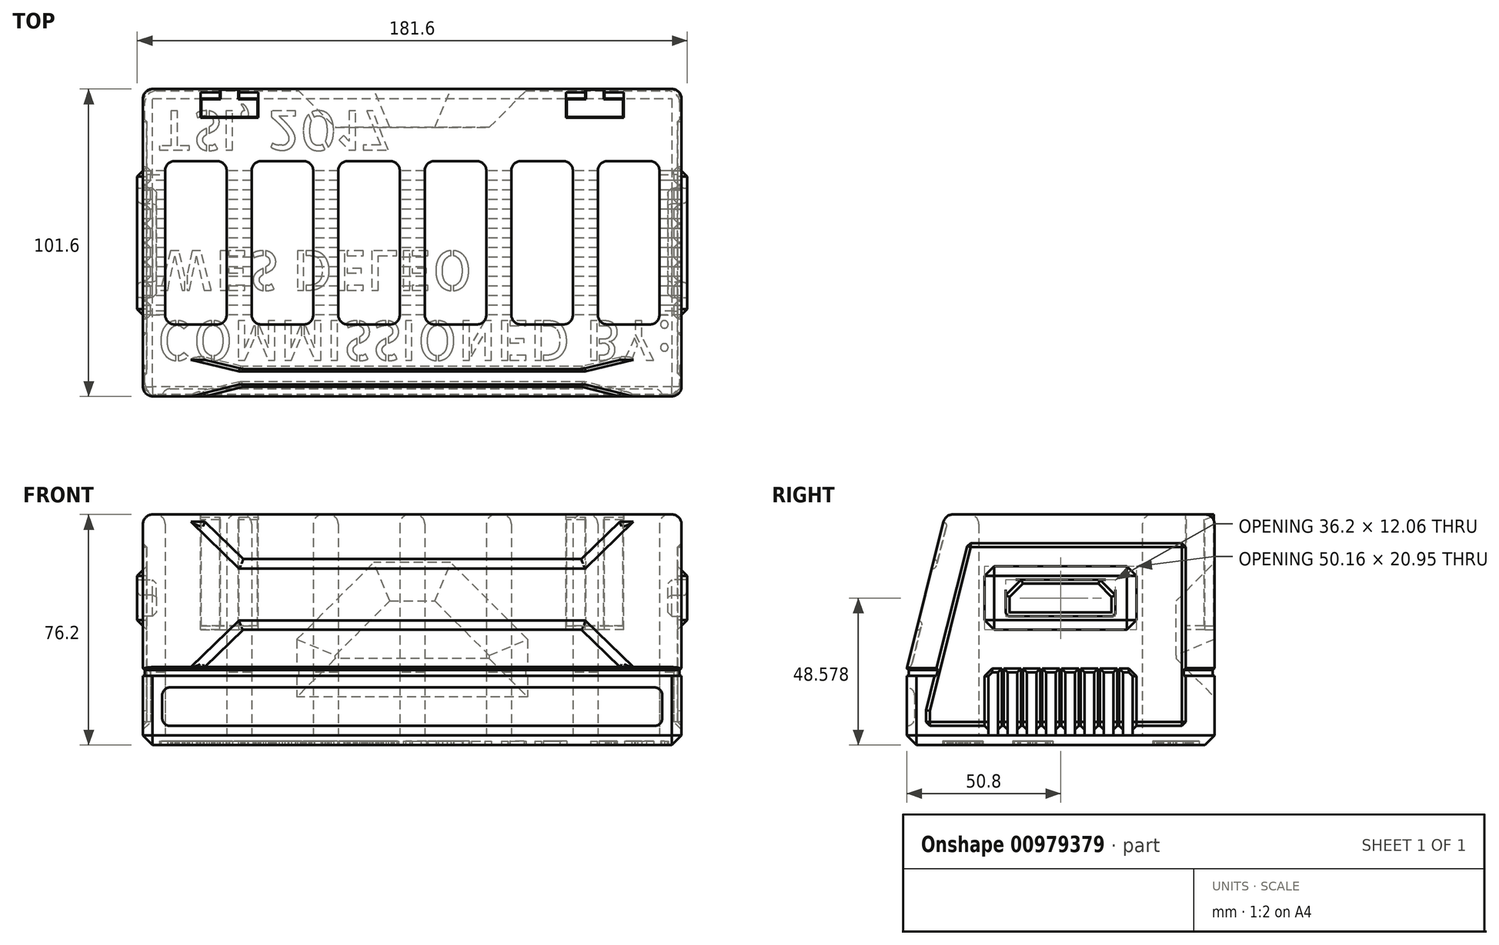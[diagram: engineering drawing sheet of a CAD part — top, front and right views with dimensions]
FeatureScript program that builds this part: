
annotation { "Feature Type Name" : "Feature", "Feature Type Description" : "" }
export const myFeature = defineFeature(function(context is Context, id is Id, definition is map)
    precondition{}
    {
        {
            var Q0;
            Q0=qCreatedBy(makeId("Top.planeOp"),FACE);
            var sketch = newSketch(context, id + "F0", { "sketchPlane" : qUnion([Q0])});
            skLineSegment(sketch, "E0.bottom", {"start": v(-81.6, 26.99) * mm, "end": v(-61.28, 26.99) * mm});
            skLineSegment(sketch, "E0.top", {"start": v(-81.6, -26.99) * mm, "end": v(-61.28, -26.99) * mm});
            skLineSegment(sketch, "E0.left", {"start": v(-81.6, 26.99) * mm, "end": v(-81.6, -26.99) * mm});
            skLineSegment(sketch, "E0.right", {"start": v(-61.28, 26.99) * mm, "end": v(-61.28, -26.99) * mm});
            skLineSegment(sketch, "E1.1.0.0", {"start": v(-53.02, 26.99) * mm, "end": v(-53.02, -26.99) * mm});
            skLineSegment(sketch, "E1.1.0.1", {"start": v(-53.02, 26.99) * mm, "end": v(-32.7, 26.99) * mm});
            skLineSegment(sketch, "E1.1.0.2", {"start": v(-32.7, 26.99) * mm, "end": v(-32.7, -26.99) * mm});
            skLineSegment(sketch, "E1.1.0.3", {"start": v(-53.02, -26.99) * mm, "end": v(-32.7, -26.99) * mm});
            skLineSegment(sketch, "E1.2.0.0", {"start": v(-24.45, 26.99) * mm, "end": v(-24.45, -26.99) * mm});
            skLineSegment(sketch, "E1.2.0.1", {"start": v(-24.45, 26.99) * mm, "end": v(-4.13, 26.99) * mm});
            skLineSegment(sketch, "E1.2.0.2", {"start": v(-4.13, 26.99) * mm, "end": v(-4.13, -26.99) * mm});
            skLineSegment(sketch, "E1.2.0.3", {"start": v(-24.45, -26.99) * mm, "end": v(-4.13, -26.99) * mm});
            skLineSegment(sketch, "E1.3.0.0", {"start": v(4.13, 26.99) * mm, "end": v(4.13, -26.99) * mm});
            skLineSegment(sketch, "E1.3.0.1", {"start": v(4.13, 26.99) * mm, "end": v(24.45, 26.99) * mm});
            skLineSegment(sketch, "E1.3.0.2", {"start": v(24.45, 26.99) * mm, "end": v(24.45, -26.99) * mm});
            skLineSegment(sketch, "E1.3.0.3", {"start": v(4.13, -26.99) * mm, "end": v(24.45, -26.99) * mm});
            skLineSegment(sketch, "E1.4.0.0", {"start": v(32.7, 26.99) * mm, "end": v(32.7, -26.99) * mm});
            skLineSegment(sketch, "E1.4.0.1", {"start": v(32.7, 26.99) * mm, "end": v(53.02, 26.99) * mm});
            skLineSegment(sketch, "E1.4.0.2", {"start": v(53.02, 26.99) * mm, "end": v(53.02, -26.99) * mm});
            skLineSegment(sketch, "E1.4.0.3", {"start": v(32.7, -26.99) * mm, "end": v(53.02, -26.99) * mm});
            skLineSegment(sketch, "E1.direction1", {"start": v(-81.6, -26.99) * mm, "end": v(-53.02, -26.99) * mm, "construction": true});
            skLineSegment(sketch, "E2.0.5.0", {"start": v(61.28, 26.99) * mm, "end": v(61.28, -26.99) * mm});
            skLineSegment(sketch, "E2.3.5.0", {"start": v(61.28, 26.99) * mm, "end": v(81.6, 26.99) * mm});
            skLineSegment(sketch, "E2.6.5.0", {"start": v(81.6, 26.99) * mm, "end": v(81.6, -26.99) * mm});
            skLineSegment(sketch, "E2.9.5.0", {"start": v(61.28, -26.99) * mm, "end": v(81.6, -26.99) * mm});
            skLineSegment(sketch, "E3.bottom", {"start": v(-88.9, 50.8) * mm, "end": v(88.9, 50.8) * mm});
            skLineSegment(sketch, "E3.top", {"start": v(-88.9, -50.8) * mm, "end": v(88.9, -50.8) * mm});
            skLineSegment(sketch, "E3.left", {"start": v(-88.9, 50.8) * mm, "end": v(-88.9, -50.8) * mm});
            skLineSegment(sketch, "E3.right", {"start": v(88.9, 50.8) * mm, "end": v(88.9, -50.8) * mm});
            skSolve(sketch);
        }
        {
            var Q0;
            Q0 = qSketchRegion(id + "F0", true);
            extrude(context, id + "F1", {"entities" : qUnion([Q0]), "depth" : 76.2 * mm, "offsetDistance" : 25.4 * mm});
        }
        {
            var Q0;
            Q0=makeQuery(id+"F1.opExtrude","CAP_EDGE",EDGE,{"disambiguationData":[OSD([sQuery(id+"F0.wireOp",EDGE,"E3.bottom")])],"isStart":false});
            chamfer(context, id + "F2", {"entities" : qUnion([Q0]), "chamferType" : ChamferType.TWO_OFFSETS, "width1" : 50.8 * mm, "oppositeDirection" : false, "width2" : 12.7 * mm, "tangentPropagation" : true});
        }
        {
            var Q0;
            Q0=makeQuery(id+"F1.opExtrude","CAP_FACE",FACE,{"disambiguationData":[OSD([sQuery(id+"F0.wireOp",EDGE,"E0.bottom"),sQuery(id+"F0.wireOp",EDGE,"E0.top"),sQuery(id+"F0.wireOp",EDGE,"E0.left"),sQuery(id+"F0.wireOp",EDGE,"E0.right"),sQuery(id+"F0.wireOp",EDGE,"E1.1.0.0"),sQuery(id+"F0.wireOp",EDGE,"E1.1.0.1"),sQuery(id+"F0.wireOp",EDGE,"E1.1.0.2"),sQuery(id+"F0.wireOp",EDGE,"E1.1.0.3"),sQuery(id+"F0.wireOp",EDGE,"E1.2.0.0"),sQuery(id+"F0.wireOp",EDGE,"E1.2.0.1"),sQuery(id+"F0.wireOp",EDGE,"E1.2.0.2"),sQuery(id+"F0.wireOp",EDGE,"E1.2.0.3"),sQuery(id+"F0.wireOp",EDGE,"E1.3.0.0"),sQuery(id+"F0.wireOp",EDGE,"E1.3.0.1"),sQuery(id+"F0.wireOp",EDGE,"E1.3.0.2"),sQuery(id+"F0.wireOp",EDGE,"E1.3.0.3"),sQuery(id+"F0.wireOp",EDGE,"E1.4.0.0"),sQuery(id+"F0.wireOp",EDGE,"E1.4.0.1"),sQuery(id+"F0.wireOp",EDGE,"E1.4.0.2"),sQuery(id+"F0.wireOp",EDGE,"E1.4.0.3"),sQuery(id+"F0.wireOp",EDGE,"E2.0.5.0"),sQuery(id+"F0.wireOp",EDGE,"E2.3.5.0"),sQuery(id+"F0.wireOp",EDGE,"E2.6.5.0"),sQuery(id+"F0.wireOp",EDGE,"E2.9.5.0"),sQuery(id+"F0.wireOp",EDGE,"E3.bottom"),sQuery(id+"F0.wireOp",EDGE,"E3.top"),sQuery(id+"F0.wireOp",EDGE,"E3.left"),sQuery(id+"F0.wireOp",EDGE,"E3.right")])],"isStart":true});
            var sketch = newSketch(context, id + "F3", { "sketchPlane" : qUnion([Q0])});
            skLineSegment(sketch, "E4.0", {"start": v(-88.9, 50.8) * mm, "end": v(88.9, 50.8) * mm});
            skLineSegment(sketch, "E5.0", {"start": v(-88.9, -50.8) * mm, "end": v(-88.9, 50.8) * mm});
            skLineSegment(sketch, "E6.0", {"start": v(-88.9, -50.8) * mm, "end": v(88.9, -50.8) * mm});
            skLineSegment(sketch, "E7.0", {"start": v(88.9, -50.8) * mm, "end": v(88.9, 50.8) * mm});
            skSolve(sketch);
        }
        {
            var Q0;
            Q0 = qSketchRegion(id + "F3", true);
            extrude(context, id + "F4", {"entities" : qUnion([Q0]), "operationType" : NewBodyOperationType.ADD, "oppositeDirection" : true, "depth" : 3.17 * mm, "offsetDistance" : 25.4 * mm});
        }
        {
            var Q0;
            Q0=makeQuery(id+"F1.opExtrude","SWEPT_FACE",FACE,{"disambiguationData":[OSD([sQuery(id+"F0.wireOp",EDGE,"E3.right")])]});
            var sketch = newSketch(context, id + "F5", { "sketchPlane" : qUnion([Q0])});
            skLineSegment(sketch, "E8.bottom", {"start": v(-23.81, 24.03) * mm, "end": v(-20.64, 24.03) * mm});
            skLineSegment(sketch, "E8.top", {"start": v(-23.81, 3.17) * mm, "end": v(-20.64, 3.17) * mm});
            skLineSegment(sketch, "E8.left", {"start": v(-23.81, 24.03) * mm, "end": v(-23.81, 3.17) * mm});
            skLineSegment(sketch, "E8.right", {"start": v(-20.64, 24.03) * mm, "end": v(-20.64, 3.18) * mm});
            skLineSegment(sketch, "E9.1.0.0", {"start": v(-17.46, 24.03) * mm, "end": v(-14.29, 24.03) * mm});
            skLineSegment(sketch, "E9.1.0.1", {"start": v(-17.46, 24.03) * mm, "end": v(-17.46, 3.17) * mm});
            skLineSegment(sketch, "E9.1.0.2", {"start": v(-17.46, 3.17) * mm, "end": v(-14.29, 3.17) * mm});
            skLineSegment(sketch, "E9.1.0.3", {"start": v(-14.29, 24.03) * mm, "end": v(-14.29, 3.17) * mm});
            skLineSegment(sketch, "E9.2.0.0", {"start": v(-11.11, 24.03) * mm, "end": v(-7.94, 24.03) * mm});
            skLineSegment(sketch, "E9.2.0.1", {"start": v(-11.11, 24.03) * mm, "end": v(-11.11, 3.17) * mm});
            skLineSegment(sketch, "E9.2.0.2", {"start": v(-11.11, 3.17) * mm, "end": v(-7.94, 3.17) * mm});
            skLineSegment(sketch, "E9.2.0.3", {"start": v(-7.94, 24.03) * mm, "end": v(-7.94, 3.17) * mm});
            skLineSegment(sketch, "E9.direction1", {"start": v(-23.81, 3.17) * mm, "end": v(-17.46, 3.17) * mm, "construction": true});
            skLineSegment(sketch, "E10.0.3.0", {"start": v(-4.76, 24.03) * mm, "end": v(-1.59, 24.03) * mm});
            skLineSegment(sketch, "E10.3.3.0", {"start": v(-4.76, 24.03) * mm, "end": v(-4.76, 3.17) * mm});
            skLineSegment(sketch, "E10.6.3.0", {"start": v(-4.76, 3.17) * mm, "end": v(-1.59, 3.17) * mm});
            skLineSegment(sketch, "E10.9.3.0", {"start": v(-1.59, 24.03) * mm, "end": v(-1.59, 3.18) * mm});
            skLineSegment(sketch, "E10.0.4.0", {"start": v(1.59, 24.03) * mm, "end": v(4.76, 24.03) * mm});
            skLineSegment(sketch, "E10.3.4.0", {"start": v(1.59, 24.03) * mm, "end": v(1.59, 3.17) * mm});
            skLineSegment(sketch, "E10.6.4.0", {"start": v(1.59, 3.17) * mm, "end": v(4.76, 3.17) * mm});
            skLineSegment(sketch, "E10.9.4.0", {"start": v(4.76, 24.03) * mm, "end": v(4.76, 3.18) * mm});
            skLineSegment(sketch, "E10.0.5.0", {"start": v(7.94, 24.03) * mm, "end": v(11.11, 24.03) * mm});
            skLineSegment(sketch, "E10.3.5.0", {"start": v(7.94, 24.03) * mm, "end": v(7.94, 3.17) * mm});
            skLineSegment(sketch, "E10.6.5.0", {"start": v(7.94, 3.17) * mm, "end": v(11.11, 3.17) * mm});
            skLineSegment(sketch, "E10.9.5.0", {"start": v(11.11, 24.03) * mm, "end": v(11.11, 3.18) * mm});
            skLineSegment(sketch, "E11.0.6.0", {"start": v(14.29, 24.03) * mm, "end": v(17.46, 24.03) * mm});
            skLineSegment(sketch, "E11.3.6.0", {"start": v(14.29, 24.03) * mm, "end": v(14.29, 3.17) * mm});
            skLineSegment(sketch, "E11.6.6.0", {"start": v(14.29, 3.17) * mm, "end": v(17.46, 3.17) * mm});
            skLineSegment(sketch, "E11.9.6.0", {"start": v(17.46, 24.03) * mm, "end": v(17.46, 3.18) * mm});
            skLineSegment(sketch, "E11.0.7.0", {"start": v(20.64, 24.03) * mm, "end": v(23.81, 24.03) * mm});
            skLineSegment(sketch, "E11.3.7.0", {"start": v(20.64, 24.03) * mm, "end": v(20.64, 3.17) * mm});
            skLineSegment(sketch, "E11.6.7.0", {"start": v(20.64, 3.17) * mm, "end": v(23.81, 3.17) * mm});
            skLineSegment(sketch, "E11.9.7.0", {"start": v(23.81, 24.03) * mm, "end": v(23.81, 3.18) * mm});
            skSolve(sketch);
        }
        {
            var Q0;
            Q0 = qSketchRegion(id + "F5", true);
            var Q1;
            Q1=makeQuery(id+"F1.opExtrude","SWEPT_FACE",FACE,{"disambiguationData":[OSD([sQuery(id+"F0.wireOp",EDGE,"E3.left")])]});
            extrude(context, id + "F6", {"entities" : qUnion([Q0]), "operationType" : NewBodyOperationType.REMOVE, "endBound" : BoundingType.UP_TO_SURFACE, "oppositeDirection" : true, "depth" : 25.4 * mm, "endBoundEntityFace" : qUnion([Q1]), "offsetDistance" : 25.4 * mm});
        }
        {
            var Q0;
            Q0=makeQuery(id+"F1.opExtrude","CAP_FACE",FACE,{"disambiguationData":[OSD([sQuery(id+"F0.wireOp",EDGE,"E0.bottom"),sQuery(id+"F0.wireOp",EDGE,"E0.top"),sQuery(id+"F0.wireOp",EDGE,"E0.left"),sQuery(id+"F0.wireOp",EDGE,"E0.right"),sQuery(id+"F0.wireOp",EDGE,"E1.1.0.0"),sQuery(id+"F0.wireOp",EDGE,"E1.1.0.1"),sQuery(id+"F0.wireOp",EDGE,"E1.1.0.2"),sQuery(id+"F0.wireOp",EDGE,"E1.1.0.3"),sQuery(id+"F0.wireOp",EDGE,"E1.2.0.0"),sQuery(id+"F0.wireOp",EDGE,"E1.2.0.1"),sQuery(id+"F0.wireOp",EDGE,"E1.2.0.2"),sQuery(id+"F0.wireOp",EDGE,"E1.2.0.3"),sQuery(id+"F0.wireOp",EDGE,"E1.3.0.0"),sQuery(id+"F0.wireOp",EDGE,"E1.3.0.1"),sQuery(id+"F0.wireOp",EDGE,"E1.3.0.2"),sQuery(id+"F0.wireOp",EDGE,"E1.3.0.3"),sQuery(id+"F0.wireOp",EDGE,"E1.4.0.0"),sQuery(id+"F0.wireOp",EDGE,"E1.4.0.1"),sQuery(id+"F0.wireOp",EDGE,"E1.4.0.2"),sQuery(id+"F0.wireOp",EDGE,"E1.4.0.3"),sQuery(id+"F0.wireOp",EDGE,"E2.0.5.0"),sQuery(id+"F0.wireOp",EDGE,"E2.3.5.0"),sQuery(id+"F0.wireOp",EDGE,"E2.6.5.0"),sQuery(id+"F0.wireOp",EDGE,"E2.9.5.0"),sQuery(id+"F0.wireOp",EDGE,"E3.bottom"),sQuery(id+"F0.wireOp",EDGE,"E3.top"),sQuery(id+"F0.wireOp",EDGE,"E3.left"),sQuery(id+"F0.wireOp",EDGE,"E3.right")])],"isStart":false});
            var Q1;
            Q1=makeQuery(id+"F1.opExtrude","SWEPT_EDGE",EDGE,{"disambiguationData":[OSD([sQuery(id+"F0.wireOp",EDGE,"E2.0.5.0"),sQuery(id+"F0.wireOp",EDGE,"E2.9.5.0")])]});
            var Q2;
            Q2=makeQuery(id+"F1.opExtrude","SWEPT_EDGE",EDGE,{"disambiguationData":[OSD([sQuery(id+"F0.wireOp",EDGE,"E1.4.0.0"),sQuery(id+"F0.wireOp",EDGE,"E1.4.0.3")])]});
            var Q3;
            Q3=makeQuery(id+"F1.opExtrude","SWEPT_EDGE",EDGE,{"disambiguationData":[OSD([sQuery(id+"F0.wireOp",EDGE,"E1.3.0.0"),sQuery(id+"F0.wireOp",EDGE,"E1.3.0.3")])]});
            var Q4;
            Q4=makeQuery(id+"F1.opExtrude","SWEPT_EDGE",EDGE,{"disambiguationData":[OSD([sQuery(id+"F0.wireOp",EDGE,"E1.2.0.0"),sQuery(id+"F0.wireOp",EDGE,"E1.2.0.3")])]});
            var Q5;
            Q5=makeQuery(id+"F1.opExtrude","SWEPT_EDGE",EDGE,{"disambiguationData":[OSD([sQuery(id+"F0.wireOp",EDGE,"E1.1.0.0"),sQuery(id+"F0.wireOp",EDGE,"E1.1.0.3")])]});
            var Q6;
            Q6=makeQuery(id+"F1.opExtrude","SWEPT_EDGE",EDGE,{"disambiguationData":[OSD([sQuery(id+"F0.wireOp",EDGE,"E0.top"),sQuery(id+"F0.wireOp",EDGE,"E0.left")])]});
            var Q7;
            Q7=makeQuery(id+"F1.opExtrude","SWEPT_EDGE",EDGE,{"disambiguationData":[OSD([sQuery(id+"F0.wireOp",EDGE,"E0.bottom"),sQuery(id+"F0.wireOp",EDGE,"E0.left")])]});
            var Q8;
            Q8=makeQuery(id+"F1.opExtrude","SWEPT_EDGE",EDGE,{"disambiguationData":[OSD([sQuery(id+"F0.wireOp",EDGE,"E0.bottom"),sQuery(id+"F0.wireOp",EDGE,"E0.right")])]});
            var Q9;
            Q9=makeQuery(id+"F1.opExtrude","SWEPT_EDGE",EDGE,{"disambiguationData":[OSD([sQuery(id+"F0.wireOp",EDGE,"E1.1.0.1"),sQuery(id+"F0.wireOp",EDGE,"E1.1.0.2")])]});
            var Q10;
            Q10=makeQuery(id+"F1.opExtrude","SWEPT_EDGE",EDGE,{"disambiguationData":[OSD([sQuery(id+"F0.wireOp",EDGE,"E1.2.0.1"),sQuery(id+"F0.wireOp",EDGE,"E1.2.0.2")])]});
            var Q11;
            Q11=makeQuery(id+"F1.opExtrude","SWEPT_EDGE",EDGE,{"disambiguationData":[OSD([sQuery(id+"F0.wireOp",EDGE,"E1.3.0.1"),sQuery(id+"F0.wireOp",EDGE,"E1.3.0.2")])]});
            var Q12;
            Q12=makeQuery(id+"F1.opExtrude","SWEPT_EDGE",EDGE,{"disambiguationData":[OSD([sQuery(id+"F0.wireOp",EDGE,"E1.4.0.1"),sQuery(id+"F0.wireOp",EDGE,"E1.4.0.2")])]});
            var Q13;
            Q13=makeQuery(id+"F1.opExtrude","SWEPT_EDGE",EDGE,{"disambiguationData":[OSD([sQuery(id+"F0.wireOp",EDGE,"E2.3.5.0"),sQuery(id+"F0.wireOp",EDGE,"E2.6.5.0")])]});
            var Q14;
            Q14=makeQuery(id+"F1.opExtrude","SWEPT_EDGE",EDGE,{"disambiguationData":[OSD([sQuery(id+"F0.wireOp",EDGE,"E2.6.5.0"),sQuery(id+"F0.wireOp",EDGE,"E2.9.5.0")])]});
            var Q15;
            Q15=makeQuery(id+"F1.opExtrude","SWEPT_EDGE",EDGE,{"disambiguationData":[OSD([sQuery(id+"F0.wireOp",EDGE,"E1.4.0.2"),sQuery(id+"F0.wireOp",EDGE,"E1.4.0.3")])]});
            var Q16;
            Q16=makeQuery(id+"F1.opExtrude","SWEPT_EDGE",EDGE,{"disambiguationData":[OSD([sQuery(id+"F0.wireOp",EDGE,"E1.3.0.2"),sQuery(id+"F0.wireOp",EDGE,"E1.3.0.3")])]});
            var Q17;
            Q17=makeQuery(id+"F1.opExtrude","SWEPT_EDGE",EDGE,{"disambiguationData":[OSD([sQuery(id+"F0.wireOp",EDGE,"E1.2.0.2"),sQuery(id+"F0.wireOp",EDGE,"E1.2.0.3")])]});
            var Q18;
            Q18=makeQuery(id+"F1.opExtrude","SWEPT_EDGE",EDGE,{"disambiguationData":[OSD([sQuery(id+"F0.wireOp",EDGE,"E1.1.0.2"),sQuery(id+"F0.wireOp",EDGE,"E1.1.0.3")])]});
            var Q19;
            Q19=makeQuery(id+"F1.opExtrude","SWEPT_EDGE",EDGE,{"disambiguationData":[OSD([sQuery(id+"F0.wireOp",EDGE,"E0.top"),sQuery(id+"F0.wireOp",EDGE,"E0.right")])]});
            var Q20;
            Q20=makeQuery(id+"F1.opExtrude","SWEPT_EDGE",EDGE,{"disambiguationData":[OSD([sQuery(id+"F0.wireOp",EDGE,"E1.1.0.0"),sQuery(id+"F0.wireOp",EDGE,"E1.1.0.1")])]});
            var Q21;
            Q21=makeQuery(id+"F1.opExtrude","SWEPT_EDGE",EDGE,{"disambiguationData":[OSD([sQuery(id+"F0.wireOp",EDGE,"E1.2.0.0"),sQuery(id+"F0.wireOp",EDGE,"E1.2.0.1")])]});
            var Q22;
            Q22=makeQuery(id+"F1.opExtrude","SWEPT_EDGE",EDGE,{"disambiguationData":[OSD([sQuery(id+"F0.wireOp",EDGE,"E1.3.0.0"),sQuery(id+"F0.wireOp",EDGE,"E1.3.0.1")])]});
            var Q23;
            Q23=makeQuery(id+"F1.opExtrude","SWEPT_EDGE",EDGE,{"disambiguationData":[OSD([sQuery(id+"F0.wireOp",EDGE,"E1.4.0.0"),sQuery(id+"F0.wireOp",EDGE,"E1.4.0.1")])]});
            var Q24;
            Q24=makeQuery(id+"F1.opExtrude","SWEPT_EDGE",EDGE,{"disambiguationData":[OSD([sQuery(id+"F0.wireOp",EDGE,"E2.0.5.0"),sQuery(id+"F0.wireOp",EDGE,"E2.3.5.0")])]});
            var Q25;
            Q25=makeQuery(id+"F2.opChamfer","BLEND_EDGE",EDGE,{"blendedFrom":[makeQuery(id+"F1.opExtrude","CAP_EDGE",EDGE,{"disambiguationData":[OSD([sQuery(id+"F0.wireOp",EDGE,"E3.bottom")])],"isStart":false}),makeQuery(id+"F1.opExtrude","SWEPT_FACE",FACE,{"disambiguationData":[OSD([sQuery(id+"F0.wireOp",EDGE,"E3.right")])]})],"blendedInto":[makeQuery(id+"F1.opExtrude","SWEPT_FACE",FACE,{"disambiguationData":[OSD([sQuery(id+"F0.wireOp",EDGE,"E3.right")])]})]});
            var Q26;
            Q26=makeQuery(id+"F2.opChamfer","BLEND_EDGE",EDGE,{"blendedFrom":[makeQuery(id+"F1.opExtrude","CAP_EDGE",EDGE,{"disambiguationData":[OSD([sQuery(id+"F0.wireOp",EDGE,"E3.bottom")])],"isStart":false}),makeQuery(id+"F1.opExtrude","SWEPT_FACE",FACE,{"disambiguationData":[OSD([sQuery(id+"F0.wireOp",EDGE,"E3.left")])]})],"blendedInto":[makeQuery(id+"F1.opExtrude","SWEPT_FACE",FACE,{"disambiguationData":[OSD([sQuery(id+"F0.wireOp",EDGE,"E3.left")])]})]});
            var Q27;
            Q27=makeQuery(id+"F1.opExtrude","SWEPT_EDGE",EDGE,{"disambiguationData":[OSD([sQuery(id+"F0.wireOp",EDGE,"E3.top"),sQuery(id+"F0.wireOp",EDGE,"E3.right")])]});
            var Q28;
            Q28=makeQuery(id+"F1.opExtrude","SWEPT_EDGE",EDGE,{"disambiguationData":[OSD([sQuery(id+"F0.wireOp",EDGE,"E3.top"),sQuery(id+"F0.wireOp",EDGE,"E3.left")])]});
            fillet(context, id + "F7", {"entities" : qUnion([Q0, Q1, Q2, Q3, Q4, Q5, Q6, Q7, Q8, Q9, Q10, Q11, Q12, Q13, Q14, Q15, Q16, Q17, Q18, Q19, Q20, Q21, Q22, Q23, Q24, Q25, Q26, Q27, Q28]), "radius" : 3.17 * mm, "tangentPropagation" : true, "allowEdgeOverflow" : false});
        }
        {
            var Q0;
            Q0=makeQuery(id+"F1.opExtrude","SWEPT_FACE",FACE,{"disambiguationData":[OSD([sQuery(id+"F0.wireOp",EDGE,"E3.left")])]});
            var sketch = newSketch(context, id + "F8", { "sketchPlane" : qUnion([Q0])});
            skLineSegment(sketch, "E12.0", {"start": v(-30.66, 66.67) * mm, "end": v(-44.45, 11.53) * mm});
            skLineSegment(sketch, "E12.1", {"start": v(41.27, 66.67) * mm, "end": v(-30.66, 66.67) * mm});
            skLineSegment(sketch, "E12.2", {"start": v(-44.45, 11.53) * mm, "end": v(-44.45, 6.35) * mm});
            skLineSegment(sketch, "E12.3", {"start": v(-44.45, 6.35) * mm, "end": v(41.27, 6.35) * mm});
            skLineSegment(sketch, "E12.4", {"start": v(41.27, 6.35) * mm, "end": v(41.27, 66.67) * mm});
            skSolve(sketch);
        }
        {
            var Q0;
            Q0 = qSketchRegion(id + "F8", true);
            extrude(context, id + "F9", {"entities" : qUnion([Q0]), "operationType" : NewBodyOperationType.REMOVE, "oppositeDirection" : true, "depth" : 1.27 * mm, "offsetDistance" : 25.4 * mm});
        }
        {
            var Q0;
            Q0=makeQuery(id+"F9.boolean.opBoolean","COPY",FACE,{"derivedFrom":makeQuery(id+"F9.opExtrude","CAP_FACE",FACE,{"disambiguationData":[OSD([sQuery(id+"F8.wireOp",EDGE,"E12.0"),sQuery(id+"F8.wireOp",EDGE,"E12.1"),sQuery(id+"F8.wireOp",EDGE,"E12.2"),sQuery(id+"F8.wireOp",EDGE,"E12.3"),sQuery(id+"F8.wireOp",EDGE,"E12.4")])],"isStart":false})});
            var Q1;
            {var subQ0=sQuery(id+"F5.wireOp",EDGE,"E11.0.7.0");var subQ1=sQuery(id+"F5.wireOp",EDGE,"E11.9.7.0");Q1=makeQuery(id+"F6.boolean.opBoolean","COPY",EDGE,{"disambiguationData":[TD([makeQuery(id+"F1.opExtrude","SWEPT_FACE",FACE,{"disambiguationData":[OSD([sQuery(id+"F0.wireOp",EDGE,"E0.left")])]})])],"derivedFrom":makeQuery(id+"F6.opExtrude","SWEPT_EDGE",EDGE,{"disambiguationData":[OSD([subQ0,subQ1])]})});}
            var Q2;
            {var subQ0=sQuery(id+"F5.wireOp",EDGE,"E8.bottom");var subQ1=sQuery(id+"F5.wireOp",EDGE,"E8.left");Q2=makeQuery(id+"F6.boolean.opBoolean","COPY",EDGE,{"disambiguationData":[TD([makeQuery(id+"F1.opExtrude","SWEPT_FACE",FACE,{"disambiguationData":[OSD([sQuery(id+"F0.wireOp",EDGE,"E0.left")])]})])],"derivedFrom":makeQuery(id+"F6.opExtrude","SWEPT_EDGE",EDGE,{"disambiguationData":[OSD([subQ0,subQ1])]})});}
            var Q3;
            Q3=makeQuery(id+"F9.boolean.opBoolean","COPY",EDGE,{"derivedFrom":makeQuery(id+"F9.opExtrude","SWEPT_EDGE",EDGE,{"disambiguationData":[OSD([sQuery(id+"F8.wireOp",EDGE,"E12.0"),sQuery(id+"F8.wireOp",EDGE,"E12.1")])]})});
            var Q4;
            Q4=makeQuery(id+"F9.boolean.opBoolean","COPY",EDGE,{"derivedFrom":makeQuery(id+"F9.opExtrude","SWEPT_EDGE",EDGE,{"disambiguationData":[OSD([sQuery(id+"F8.wireOp",EDGE,"E12.1"),sQuery(id+"F8.wireOp",EDGE,"E12.4")])]})});
            var Q5;
            Q5=makeQuery(id+"F9.boolean.opBoolean","COPY",EDGE,{"derivedFrom":makeQuery(id+"F9.opExtrude","SWEPT_EDGE",EDGE,{"disambiguationData":[OSD([sQuery(id+"F8.wireOp",EDGE,"E12.3"),sQuery(id+"F8.wireOp",EDGE,"E12.4")])]})});
            var Q6;
            Q6=makeQuery(id+"F9.boolean.opBoolean","COPY",EDGE,{"derivedFrom":makeQuery(id+"F9.opExtrude","SWEPT_EDGE",EDGE,{"disambiguationData":[OSD([sQuery(id+"F8.wireOp",EDGE,"E12.2"),sQuery(id+"F8.wireOp",EDGE,"E12.3")])]})});
            chamfer(context, id + "F10", {"entities" : qUnion([Q0, Q1, Q2, Q3, Q4, Q5, Q6]), "width" : 1.27 * mm, "tangentPropagation" : true});
        }
        {
            var Q0;
            Q0=makeQuery(id+"F1.opExtrude","SWEPT_FACE",FACE,{"disambiguationData":[OSD([sQuery(id+"F0.wireOp",EDGE,"E3.right")])]});
            var sketch = newSketch(context, id + "F11", { "sketchPlane" : qUnion([Q0])});
            skLineSegment(sketch, "E13.0", {"start": v(44.45, 11.53) * mm, "end": v(30.66, 66.68) * mm});
            skLineSegment(sketch, "E13.1", {"start": v(44.45, 6.35) * mm, "end": v(44.45, 11.53) * mm});
            skLineSegment(sketch, "E13.2", {"start": v(30.66, 66.68) * mm, "end": v(-41.27, 66.68) * mm});
            skLineSegment(sketch, "E13.3", {"start": v(-41.27, 66.68) * mm, "end": v(-41.27, 6.35) * mm});
            skLineSegment(sketch, "E13.4", {"start": v(-41.27, 6.35) * mm, "end": v(44.45, 6.35) * mm});
            skSolve(sketch);
        }
        {
            var Q0;
            Q0 = qSketchRegion(id + "F11", true);
            extrude(context, id + "F12", {"entities" : qUnion([Q0]), "operationType" : NewBodyOperationType.REMOVE, "oppositeDirection" : true, "depth" : 1.27 * mm, "offsetDistance" : 25.4 * mm});
        }
        {
            var Q0;
            Q0=makeQuery(id+"F12.boolean.opBoolean","COPY",FACE,{"derivedFrom":makeQuery(id+"F12.opExtrude","CAP_FACE",FACE,{"disambiguationData":[OSD([sQuery(id+"F11.wireOp",EDGE,"E13.0"),sQuery(id+"F11.wireOp",EDGE,"E13.1"),sQuery(id+"F11.wireOp",EDGE,"E13.2"),sQuery(id+"F11.wireOp",EDGE,"E13.3"),sQuery(id+"F11.wireOp",EDGE,"E13.4")])],"isStart":false})});
            var Q1;
            {var subQ0=sQuery(id+"F5.wireOp",EDGE,"E8.bottom");var subQ1=sQuery(id+"F5.wireOp",EDGE,"E8.left");Q1=makeQuery(id+"F6.boolean.opBoolean","COPY",EDGE,{"disambiguationData":[TD([makeQuery(id+"F1.opExtrude","SWEPT_FACE",FACE,{"disambiguationData":[OSD([sQuery(id+"F0.wireOp",EDGE,"E2.6.5.0")])]})])],"derivedFrom":makeQuery(id+"F6.opExtrude","SWEPT_EDGE",EDGE,{"disambiguationData":[OSD([subQ0,subQ1])]})});}
            var Q2;
            {var subQ0=sQuery(id+"F5.wireOp",EDGE,"E11.0.7.0");var subQ1=sQuery(id+"F5.wireOp",EDGE,"E11.9.7.0");Q2=makeQuery(id+"F6.boolean.opBoolean","COPY",EDGE,{"disambiguationData":[TD([makeQuery(id+"F1.opExtrude","SWEPT_FACE",FACE,{"disambiguationData":[OSD([sQuery(id+"F0.wireOp",EDGE,"E2.6.5.0")])]})])],"derivedFrom":makeQuery(id+"F6.opExtrude","SWEPT_EDGE",EDGE,{"disambiguationData":[OSD([subQ0,subQ1])]})});}
            var Q3;
            Q3=makeQuery(id+"F12.boolean.opBoolean","COPY",EDGE,{"derivedFrom":makeQuery(id+"F12.opExtrude","SWEPT_EDGE",EDGE,{"disambiguationData":[OSD([sQuery(id+"F11.wireOp",EDGE,"E13.2"),sQuery(id+"F11.wireOp",EDGE,"E13.3")])]})});
            var Q4;
            Q4=makeQuery(id+"F12.boolean.opBoolean","COPY",EDGE,{"derivedFrom":makeQuery(id+"F12.opExtrude","SWEPT_EDGE",EDGE,{"disambiguationData":[OSD([sQuery(id+"F11.wireOp",EDGE,"E13.0"),sQuery(id+"F11.wireOp",EDGE,"E13.2")])]})});
            var Q5;
            Q5=makeQuery(id+"F12.boolean.opBoolean","COPY",EDGE,{"derivedFrom":makeQuery(id+"F12.opExtrude","SWEPT_EDGE",EDGE,{"disambiguationData":[OSD([sQuery(id+"F11.wireOp",EDGE,"E13.1"),sQuery(id+"F11.wireOp",EDGE,"E13.4")])]})});
            var Q6;
            Q6=makeQuery(id+"F12.boolean.opBoolean","COPY",EDGE,{"derivedFrom":makeQuery(id+"F12.opExtrude","SWEPT_EDGE",EDGE,{"disambiguationData":[OSD([sQuery(id+"F11.wireOp",EDGE,"E13.3"),sQuery(id+"F11.wireOp",EDGE,"E13.4")])]})});
            chamfer(context, id + "F13", {"entities" : qUnion([Q0, Q1, Q2, Q3, Q4, Q5, Q6]), "width" : 1.27 * mm, "tangentPropagation" : true});
        }
        {
            var Q0;
            Q0=makeQuery(id+"F1.opExtrude","SWEPT_FACE",FACE,{"disambiguationData":[OSD([sQuery(id+"F0.wireOp",EDGE,"E3.bottom")])]});
            var sketch = newSketch(context, id + "F14", { "sketchPlane" : qUnion([Q0])});
            skLineSegment(sketch, "E14.bottom", {"start": v(-82.55, 19.05) * mm, "end": v(82.55, 19.05) * mm});
            skLineSegment(sketch, "E14.top", {"start": v(-82.55, 6.35) * mm, "end": v(82.55, 6.35) * mm});
            skLineSegment(sketch, "E14.left", {"start": v(-82.55, 19.05) * mm, "end": v(-82.55, 6.35) * mm});
            skLineSegment(sketch, "E14.right", {"start": v(82.55, 19.05) * mm, "end": v(82.55, 6.35) * mm});
            skSolve(sketch);
        }
        {
            var Q0;
            Q0=makeQuery(id+"F14.imprint","IMPRINT",FACE,{"disambiguationData":[TD([[makeQuery(id+"F14.imprint","IMPRINT",EDGE,{"derivedFrom":sQuery(id+"F14.wireOp",EDGE,"E14.bottom")}),-1.0]])]});
            extrude(context, id + "F15", {"entities" : qUnion([Q0]), "operationType" : NewBodyOperationType.REMOVE, "oppositeDirection" : true, "depth" : 2.54 * mm, "offsetDistance" : 25.4 * mm});
        }
        {
            var Q0;
            Q0=makeQuery(id+"F15.boolean.opBoolean","COPY",EDGE,{"derivedFrom":makeQuery(id+"F15.opExtrude","SWEPT_EDGE",EDGE,{"disambiguationData":[OSD([sQuery(id+"F14.wireOp",EDGE,"E14.bottom"),sQuery(id+"F14.wireOp",EDGE,"E14.left")])]})});
            var Q1;
            Q1=makeQuery(id+"F15.boolean.opBoolean","COPY",EDGE,{"derivedFrom":makeQuery(id+"F15.opExtrude","SWEPT_EDGE",EDGE,{"disambiguationData":[OSD([sQuery(id+"F14.wireOp",EDGE,"E14.bottom"),sQuery(id+"F14.wireOp",EDGE,"E14.right")])]})});
            var Q2;
            Q2=makeQuery(id+"F15.boolean.opBoolean","COPY",FACE,{"derivedFrom":makeQuery(id+"F15.opExtrude","CAP_FACE",FACE,{"disambiguationData":[OSD([sQuery(id+"F14.wireOp",EDGE,"E14.bottom"),sQuery(id+"F14.wireOp",EDGE,"E14.top"),sQuery(id+"F14.wireOp",EDGE,"E14.left"),sQuery(id+"F14.wireOp",EDGE,"E14.right")])],"isStart":false})});
            var Q3;
            Q3=makeQuery(id+"F15.boolean.opBoolean","COPY",EDGE,{"derivedFrom":makeQuery(id+"F15.opExtrude","SWEPT_EDGE",EDGE,{"disambiguationData":[OSD([sQuery(id+"F14.wireOp",EDGE,"E14.top"),sQuery(id+"F14.wireOp",EDGE,"E14.left")])]})});
            var Q4;
            Q4=makeQuery(id+"F15.boolean.opBoolean","COPY",EDGE,{"derivedFrom":makeQuery(id+"F15.opExtrude","SWEPT_EDGE",EDGE,{"disambiguationData":[OSD([sQuery(id+"F14.wireOp",EDGE,"E14.top"),sQuery(id+"F14.wireOp",EDGE,"E14.right")])]})});
            fillet(context, id + "F16", {"entities" : qUnion([Q0, Q1, Q2, Q3, Q4]), "radius" : 2.54 * mm, "tangentPropagation" : true, "allowEdgeOverflow" : false});
        }
        {
            var Q0;
            Q0=makeQuery(id+"F1.opExtrude","CAP_FACE",FACE,{"disambiguationData":[OSD([sQuery(id+"F0.wireOp",EDGE,"E0.bottom"),sQuery(id+"F0.wireOp",EDGE,"E0.top"),sQuery(id+"F0.wireOp",EDGE,"E0.left"),sQuery(id+"F0.wireOp",EDGE,"E0.right"),sQuery(id+"F0.wireOp",EDGE,"E1.1.0.0"),sQuery(id+"F0.wireOp",EDGE,"E1.1.0.1"),sQuery(id+"F0.wireOp",EDGE,"E1.1.0.2"),sQuery(id+"F0.wireOp",EDGE,"E1.1.0.3"),sQuery(id+"F0.wireOp",EDGE,"E1.2.0.0"),sQuery(id+"F0.wireOp",EDGE,"E1.2.0.1"),sQuery(id+"F0.wireOp",EDGE,"E1.2.0.2"),sQuery(id+"F0.wireOp",EDGE,"E1.2.0.3"),sQuery(id+"F0.wireOp",EDGE,"E1.3.0.0"),sQuery(id+"F0.wireOp",EDGE,"E1.3.0.1"),sQuery(id+"F0.wireOp",EDGE,"E1.3.0.2"),sQuery(id+"F0.wireOp",EDGE,"E1.3.0.3"),sQuery(id+"F0.wireOp",EDGE,"E1.4.0.0"),sQuery(id+"F0.wireOp",EDGE,"E1.4.0.1"),sQuery(id+"F0.wireOp",EDGE,"E1.4.0.2"),sQuery(id+"F0.wireOp",EDGE,"E1.4.0.3"),sQuery(id+"F0.wireOp",EDGE,"E2.0.5.0"),sQuery(id+"F0.wireOp",EDGE,"E2.3.5.0"),sQuery(id+"F0.wireOp",EDGE,"E2.6.5.0"),sQuery(id+"F0.wireOp",EDGE,"E2.9.5.0"),sQuery(id+"F0.wireOp",EDGE,"E3.bottom"),sQuery(id+"F0.wireOp",EDGE,"E3.top"),sQuery(id+"F0.wireOp",EDGE,"E3.left"),sQuery(id+"F0.wireOp",EDGE,"E3.right")])],"isStart":false});
            var sketch = newSketch(context, id + "F17", { "sketchPlane" : qUnion([Q0])});
            skLineSegment(sketch, "E15", {"start": v(-69.85, -47.63) * mm, "end": v(-69.85, -41.28) * mm});
            skLineSegment(sketch, "E16", {"start": v(-69.85, -41.28) * mm, "end": v(-50.8, -41.28) * mm});
            skLineSegment(sketch, "E17", {"start": v(-50.8, -41.28) * mm, "end": v(-50.8, -47.63) * mm});
            skLineSegment(sketch, "E18", {"start": v(-50.8, -47.63) * mm, "end": v(-57.15, -47.63) * mm});
            skLineSegment(sketch, "E19", {"start": v(-57.15, -47.63) * mm, "end": v(-57.15, -50.8) * mm});
            skLineSegment(sketch, "E20", {"start": v(-69.85, -47.63) * mm, "end": v(-63.5, -47.63) * mm});
            skLineSegment(sketch, "E21", {"start": v(-63.5, -47.63) * mm, "end": v(-63.5, -50.8) * mm});
            skLineSegment(sketch, "E22", {"start": v(-63.5, -50.8) * mm, "end": v(-57.15, -50.8) * mm});
            skLineSegment(sketch, "E23.MirrorCS", {"start": v(63.5, -47.63) * mm, "end": v(63.5, -50.8) * mm});
            skLineSegment(sketch, "E24.MirrorCS", {"start": v(57.15, -47.63) * mm, "end": v(57.15, -50.8) * mm});
            skLineSegment(sketch, "E25.MirrorCS", {"start": v(63.5, -50.8) * mm, "end": v(57.15, -50.8) * mm});
            skLineSegment(sketch, "E26.MirrorCS", {"start": v(69.85, -47.63) * mm, "end": v(69.85, -41.28) * mm});
            skLineSegment(sketch, "E27.MirrorCS", {"start": v(69.85, -47.63) * mm, "end": v(63.5, -47.63) * mm});
            skLineSegment(sketch, "E28.MirrorCS", {"start": v(50.8, -47.63) * mm, "end": v(57.15, -47.63) * mm});
            skLineSegment(sketch, "E29.MirrorCS", {"start": v(69.85, -41.28) * mm, "end": v(50.8, -41.28) * mm});
            skLineSegment(sketch, "E30.MirrorCS", {"start": v(50.8, -41.28) * mm, "end": v(50.8, -47.63) * mm});
            skSolve(sketch);
        }
        {
            var Q0;
            Q0 = qSketchRegion(id + "F17", true);
            extrude(context, id + "F18", {"entities" : qUnion([Q0]), "operationType" : NewBodyOperationType.REMOVE, "oppositeDirection" : true, "depth" : 38.1 * mm, "offsetDistance" : 25.4 * mm});
        }
        {
            var Q0;
            Q0=makeQuery(id+"F18.boolean.opBoolean","COPY",EDGE,{"derivedFrom":makeQuery(id+"F18.opExtrude","CAP_EDGE",EDGE,{"disambiguationData":[OSD([sQuery(id+"F17.wireOp",EDGE,"E16")])],"isStart":true})});
            var Q1;
            Q1=makeQuery(id+"F18.boolean.opBoolean","COPY",EDGE,{"derivedFrom":makeQuery(id+"F18.opExtrude","CAP_EDGE",EDGE,{"disambiguationData":[OSD([sQuery(id+"F17.wireOp",EDGE,"E17")])],"isStart":true})});
            var Q2;
            {var subQ0=sQuery(id+"F0.wireOp",EDGE,"E3.top");Q2=makeQuery(id+"F18.boolean.opBoolean","MERGE",EDGE,{"derivedFrom":[makeQuery(id+"F7.opFillet","BLEND_EDGE",EDGE,{"blendedFrom":[makeQuery(id+"F1.opExtrude","CAP_EDGE",EDGE,{"disambiguationData":[OSD([subQ0])],"isStart":false}),makeQuery(id+"F1.opExtrude","CAP_FACE",FACE,{"disambiguationData":[OSD([sQuery(id+"F0.wireOp",EDGE,"E0.bottom"),sQuery(id+"F0.wireOp",EDGE,"E0.top"),sQuery(id+"F0.wireOp",EDGE,"E0.left"),sQuery(id+"F0.wireOp",EDGE,"E0.right"),sQuery(id+"F0.wireOp",EDGE,"E1.1.0.0"),sQuery(id+"F0.wireOp",EDGE,"E1.1.0.1"),sQuery(id+"F0.wireOp",EDGE,"E1.1.0.2"),sQuery(id+"F0.wireOp",EDGE,"E1.1.0.3"),sQuery(id+"F0.wireOp",EDGE,"E1.2.0.0"),sQuery(id+"F0.wireOp",EDGE,"E1.2.0.1"),sQuery(id+"F0.wireOp",EDGE,"E1.2.0.2"),sQuery(id+"F0.wireOp",EDGE,"E1.2.0.3"),sQuery(id+"F0.wireOp",EDGE,"E1.3.0.0"),sQuery(id+"F0.wireOp",EDGE,"E1.3.0.1"),sQuery(id+"F0.wireOp",EDGE,"E1.3.0.2"),sQuery(id+"F0.wireOp",EDGE,"E1.3.0.3"),sQuery(id+"F0.wireOp",EDGE,"E1.4.0.0"),sQuery(id+"F0.wireOp",EDGE,"E1.4.0.1"),sQuery(id+"F0.wireOp",EDGE,"E1.4.0.2"),sQuery(id+"F0.wireOp",EDGE,"E1.4.0.3"),sQuery(id+"F0.wireOp",EDGE,"E2.0.5.0"),sQuery(id+"F0.wireOp",EDGE,"E2.3.5.0"),sQuery(id+"F0.wireOp",EDGE,"E2.6.5.0"),sQuery(id+"F0.wireOp",EDGE,"E2.9.5.0"),sQuery(id+"F0.wireOp",EDGE,"E3.bottom"),subQ0,sQuery(id+"F0.wireOp",EDGE,"E3.left"),sQuery(id+"F0.wireOp",EDGE,"E3.right")])],"isStart":false})],"blendedInto":[makeQuery(id+"F1.opExtrude","CAP_FACE",FACE,{"disambiguationData":[OSD([sQuery(id+"F0.wireOp",EDGE,"E0.bottom"),sQuery(id+"F0.wireOp",EDGE,"E0.top"),sQuery(id+"F0.wireOp",EDGE,"E0.left"),sQuery(id+"F0.wireOp",EDGE,"E0.right"),sQuery(id+"F0.wireOp",EDGE,"E1.1.0.0"),sQuery(id+"F0.wireOp",EDGE,"E1.1.0.1"),sQuery(id+"F0.wireOp",EDGE,"E1.1.0.2"),sQuery(id+"F0.wireOp",EDGE,"E1.1.0.3"),sQuery(id+"F0.wireOp",EDGE,"E1.2.0.0"),sQuery(id+"F0.wireOp",EDGE,"E1.2.0.1"),sQuery(id+"F0.wireOp",EDGE,"E1.2.0.2"),sQuery(id+"F0.wireOp",EDGE,"E1.2.0.3"),sQuery(id+"F0.wireOp",EDGE,"E1.3.0.0"),sQuery(id+"F0.wireOp",EDGE,"E1.3.0.1"),sQuery(id+"F0.wireOp",EDGE,"E1.3.0.2"),sQuery(id+"F0.wireOp",EDGE,"E1.3.0.3"),sQuery(id+"F0.wireOp",EDGE,"E1.4.0.0"),sQuery(id+"F0.wireOp",EDGE,"E1.4.0.1"),sQuery(id+"F0.wireOp",EDGE,"E1.4.0.2"),sQuery(id+"F0.wireOp",EDGE,"E1.4.0.3"),sQuery(id+"F0.wireOp",EDGE,"E2.0.5.0"),sQuery(id+"F0.wireOp",EDGE,"E2.3.5.0"),sQuery(id+"F0.wireOp",EDGE,"E2.6.5.0"),sQuery(id+"F0.wireOp",EDGE,"E2.9.5.0"),sQuery(id+"F0.wireOp",EDGE,"E3.bottom"),subQ0,sQuery(id+"F0.wireOp",EDGE,"E3.left"),sQuery(id+"F0.wireOp",EDGE,"E3.right")])],"isStart":false})]})],"fromTools":[makeQuery(id+"F18.opExtrude","CAP_EDGE",EDGE,{"disambiguationData":[OSD([sQuery(id+"F17.wireOp",EDGE,"E18")])],"isStart":true})]});}
            var Q3;
            {var subQ0=sQuery(id+"F0.wireOp",EDGE,"E3.top");Q3=makeQuery(id+"F18.boolean.opBoolean","MERGE",EDGE,{"derivedFrom":[makeQuery(id+"F7.opFillet","BLEND_EDGE",EDGE,{"blendedFrom":[makeQuery(id+"F1.opExtrude","CAP_EDGE",EDGE,{"disambiguationData":[OSD([subQ0])],"isStart":false}),makeQuery(id+"F1.opExtrude","CAP_FACE",FACE,{"disambiguationData":[OSD([sQuery(id+"F0.wireOp",EDGE,"E0.bottom"),sQuery(id+"F0.wireOp",EDGE,"E0.top"),sQuery(id+"F0.wireOp",EDGE,"E0.left"),sQuery(id+"F0.wireOp",EDGE,"E0.right"),sQuery(id+"F0.wireOp",EDGE,"E1.1.0.0"),sQuery(id+"F0.wireOp",EDGE,"E1.1.0.1"),sQuery(id+"F0.wireOp",EDGE,"E1.1.0.2"),sQuery(id+"F0.wireOp",EDGE,"E1.1.0.3"),sQuery(id+"F0.wireOp",EDGE,"E1.2.0.0"),sQuery(id+"F0.wireOp",EDGE,"E1.2.0.1"),sQuery(id+"F0.wireOp",EDGE,"E1.2.0.2"),sQuery(id+"F0.wireOp",EDGE,"E1.2.0.3"),sQuery(id+"F0.wireOp",EDGE,"E1.3.0.0"),sQuery(id+"F0.wireOp",EDGE,"E1.3.0.1"),sQuery(id+"F0.wireOp",EDGE,"E1.3.0.2"),sQuery(id+"F0.wireOp",EDGE,"E1.3.0.3"),sQuery(id+"F0.wireOp",EDGE,"E1.4.0.0"),sQuery(id+"F0.wireOp",EDGE,"E1.4.0.1"),sQuery(id+"F0.wireOp",EDGE,"E1.4.0.2"),sQuery(id+"F0.wireOp",EDGE,"E1.4.0.3"),sQuery(id+"F0.wireOp",EDGE,"E2.0.5.0"),sQuery(id+"F0.wireOp",EDGE,"E2.3.5.0"),sQuery(id+"F0.wireOp",EDGE,"E2.6.5.0"),sQuery(id+"F0.wireOp",EDGE,"E2.9.5.0"),sQuery(id+"F0.wireOp",EDGE,"E3.bottom"),subQ0,sQuery(id+"F0.wireOp",EDGE,"E3.left"),sQuery(id+"F0.wireOp",EDGE,"E3.right")])],"isStart":false})],"blendedInto":[makeQuery(id+"F1.opExtrude","CAP_FACE",FACE,{"disambiguationData":[OSD([sQuery(id+"F0.wireOp",EDGE,"E0.bottom"),sQuery(id+"F0.wireOp",EDGE,"E0.top"),sQuery(id+"F0.wireOp",EDGE,"E0.left"),sQuery(id+"F0.wireOp",EDGE,"E0.right"),sQuery(id+"F0.wireOp",EDGE,"E1.1.0.0"),sQuery(id+"F0.wireOp",EDGE,"E1.1.0.1"),sQuery(id+"F0.wireOp",EDGE,"E1.1.0.2"),sQuery(id+"F0.wireOp",EDGE,"E1.1.0.3"),sQuery(id+"F0.wireOp",EDGE,"E1.2.0.0"),sQuery(id+"F0.wireOp",EDGE,"E1.2.0.1"),sQuery(id+"F0.wireOp",EDGE,"E1.2.0.2"),sQuery(id+"F0.wireOp",EDGE,"E1.2.0.3"),sQuery(id+"F0.wireOp",EDGE,"E1.3.0.0"),sQuery(id+"F0.wireOp",EDGE,"E1.3.0.1"),sQuery(id+"F0.wireOp",EDGE,"E1.3.0.2"),sQuery(id+"F0.wireOp",EDGE,"E1.3.0.3"),sQuery(id+"F0.wireOp",EDGE,"E1.4.0.0"),sQuery(id+"F0.wireOp",EDGE,"E1.4.0.1"),sQuery(id+"F0.wireOp",EDGE,"E1.4.0.2"),sQuery(id+"F0.wireOp",EDGE,"E1.4.0.3"),sQuery(id+"F0.wireOp",EDGE,"E2.0.5.0"),sQuery(id+"F0.wireOp",EDGE,"E2.3.5.0"),sQuery(id+"F0.wireOp",EDGE,"E2.6.5.0"),sQuery(id+"F0.wireOp",EDGE,"E2.9.5.0"),sQuery(id+"F0.wireOp",EDGE,"E3.bottom"),subQ0,sQuery(id+"F0.wireOp",EDGE,"E3.left"),sQuery(id+"F0.wireOp",EDGE,"E3.right")])],"isStart":false})]})],"fromTools":[makeQuery(id+"F18.opExtrude","CAP_EDGE",EDGE,{"disambiguationData":[OSD([sQuery(id+"F17.wireOp",EDGE,"E20")])],"isStart":true})]});}
            var Q4;
            Q4=makeQuery(id+"F18.boolean.opBoolean","COPY",EDGE,{"derivedFrom":makeQuery(id+"F18.opExtrude","CAP_EDGE",EDGE,{"disambiguationData":[OSD([sQuery(id+"F17.wireOp",EDGE,"E15")])],"isStart":true})});
            var Q5;
            Q5=makeQuery(id+"F18.boolean.opBoolean","COPY",EDGE,{"derivedFrom":makeQuery(id+"F18.opExtrude","CAP_EDGE",EDGE,{"disambiguationData":[OSD([sQuery(id+"F17.wireOp",EDGE,"E29.MirrorCS")])],"isStart":true})});
            var Q6;
            Q6=makeQuery(id+"F18.boolean.opBoolean","COPY",EDGE,{"derivedFrom":makeQuery(id+"F18.opExtrude","CAP_EDGE",EDGE,{"disambiguationData":[OSD([sQuery(id+"F17.wireOp",EDGE,"E30.MirrorCS")])],"isStart":true})});
            var Q7;
            {var subQ0=sQuery(id+"F0.wireOp",EDGE,"E3.top");Q7=makeQuery(id+"F18.boolean.opBoolean","MERGE",EDGE,{"derivedFrom":[makeQuery(id+"F7.opFillet","BLEND_EDGE",EDGE,{"blendedFrom":[makeQuery(id+"F1.opExtrude","CAP_EDGE",EDGE,{"disambiguationData":[OSD([subQ0])],"isStart":false}),makeQuery(id+"F1.opExtrude","CAP_FACE",FACE,{"disambiguationData":[OSD([sQuery(id+"F0.wireOp",EDGE,"E0.bottom"),sQuery(id+"F0.wireOp",EDGE,"E0.top"),sQuery(id+"F0.wireOp",EDGE,"E0.left"),sQuery(id+"F0.wireOp",EDGE,"E0.right"),sQuery(id+"F0.wireOp",EDGE,"E1.1.0.0"),sQuery(id+"F0.wireOp",EDGE,"E1.1.0.1"),sQuery(id+"F0.wireOp",EDGE,"E1.1.0.2"),sQuery(id+"F0.wireOp",EDGE,"E1.1.0.3"),sQuery(id+"F0.wireOp",EDGE,"E1.2.0.0"),sQuery(id+"F0.wireOp",EDGE,"E1.2.0.1"),sQuery(id+"F0.wireOp",EDGE,"E1.2.0.2"),sQuery(id+"F0.wireOp",EDGE,"E1.2.0.3"),sQuery(id+"F0.wireOp",EDGE,"E1.3.0.0"),sQuery(id+"F0.wireOp",EDGE,"E1.3.0.1"),sQuery(id+"F0.wireOp",EDGE,"E1.3.0.2"),sQuery(id+"F0.wireOp",EDGE,"E1.3.0.3"),sQuery(id+"F0.wireOp",EDGE,"E1.4.0.0"),sQuery(id+"F0.wireOp",EDGE,"E1.4.0.1"),sQuery(id+"F0.wireOp",EDGE,"E1.4.0.2"),sQuery(id+"F0.wireOp",EDGE,"E1.4.0.3"),sQuery(id+"F0.wireOp",EDGE,"E2.0.5.0"),sQuery(id+"F0.wireOp",EDGE,"E2.3.5.0"),sQuery(id+"F0.wireOp",EDGE,"E2.6.5.0"),sQuery(id+"F0.wireOp",EDGE,"E2.9.5.0"),sQuery(id+"F0.wireOp",EDGE,"E3.bottom"),subQ0,sQuery(id+"F0.wireOp",EDGE,"E3.left"),sQuery(id+"F0.wireOp",EDGE,"E3.right")])],"isStart":false})],"blendedInto":[makeQuery(id+"F1.opExtrude","CAP_FACE",FACE,{"disambiguationData":[OSD([sQuery(id+"F0.wireOp",EDGE,"E0.bottom"),sQuery(id+"F0.wireOp",EDGE,"E0.top"),sQuery(id+"F0.wireOp",EDGE,"E0.left"),sQuery(id+"F0.wireOp",EDGE,"E0.right"),sQuery(id+"F0.wireOp",EDGE,"E1.1.0.0"),sQuery(id+"F0.wireOp",EDGE,"E1.1.0.1"),sQuery(id+"F0.wireOp",EDGE,"E1.1.0.2"),sQuery(id+"F0.wireOp",EDGE,"E1.1.0.3"),sQuery(id+"F0.wireOp",EDGE,"E1.2.0.0"),sQuery(id+"F0.wireOp",EDGE,"E1.2.0.1"),sQuery(id+"F0.wireOp",EDGE,"E1.2.0.2"),sQuery(id+"F0.wireOp",EDGE,"E1.2.0.3"),sQuery(id+"F0.wireOp",EDGE,"E1.3.0.0"),sQuery(id+"F0.wireOp",EDGE,"E1.3.0.1"),sQuery(id+"F0.wireOp",EDGE,"E1.3.0.2"),sQuery(id+"F0.wireOp",EDGE,"E1.3.0.3"),sQuery(id+"F0.wireOp",EDGE,"E1.4.0.0"),sQuery(id+"F0.wireOp",EDGE,"E1.4.0.1"),sQuery(id+"F0.wireOp",EDGE,"E1.4.0.2"),sQuery(id+"F0.wireOp",EDGE,"E1.4.0.3"),sQuery(id+"F0.wireOp",EDGE,"E2.0.5.0"),sQuery(id+"F0.wireOp",EDGE,"E2.3.5.0"),sQuery(id+"F0.wireOp",EDGE,"E2.6.5.0"),sQuery(id+"F0.wireOp",EDGE,"E2.9.5.0"),sQuery(id+"F0.wireOp",EDGE,"E3.bottom"),subQ0,sQuery(id+"F0.wireOp",EDGE,"E3.left"),sQuery(id+"F0.wireOp",EDGE,"E3.right")])],"isStart":false})]})],"fromTools":[makeQuery(id+"F18.opExtrude","CAP_EDGE",EDGE,{"disambiguationData":[OSD([sQuery(id+"F17.wireOp",EDGE,"E28.MirrorCS")])],"isStart":true})]});}
            var Q8;
            {var subQ0=sQuery(id+"F0.wireOp",EDGE,"E3.top");Q8=makeQuery(id+"F18.boolean.opBoolean","MERGE",EDGE,{"derivedFrom":[makeQuery(id+"F7.opFillet","BLEND_EDGE",EDGE,{"blendedFrom":[makeQuery(id+"F1.opExtrude","CAP_EDGE",EDGE,{"disambiguationData":[OSD([subQ0])],"isStart":false}),makeQuery(id+"F1.opExtrude","CAP_FACE",FACE,{"disambiguationData":[OSD([sQuery(id+"F0.wireOp",EDGE,"E0.bottom"),sQuery(id+"F0.wireOp",EDGE,"E0.top"),sQuery(id+"F0.wireOp",EDGE,"E0.left"),sQuery(id+"F0.wireOp",EDGE,"E0.right"),sQuery(id+"F0.wireOp",EDGE,"E1.1.0.0"),sQuery(id+"F0.wireOp",EDGE,"E1.1.0.1"),sQuery(id+"F0.wireOp",EDGE,"E1.1.0.2"),sQuery(id+"F0.wireOp",EDGE,"E1.1.0.3"),sQuery(id+"F0.wireOp",EDGE,"E1.2.0.0"),sQuery(id+"F0.wireOp",EDGE,"E1.2.0.1"),sQuery(id+"F0.wireOp",EDGE,"E1.2.0.2"),sQuery(id+"F0.wireOp",EDGE,"E1.2.0.3"),sQuery(id+"F0.wireOp",EDGE,"E1.3.0.0"),sQuery(id+"F0.wireOp",EDGE,"E1.3.0.1"),sQuery(id+"F0.wireOp",EDGE,"E1.3.0.2"),sQuery(id+"F0.wireOp",EDGE,"E1.3.0.3"),sQuery(id+"F0.wireOp",EDGE,"E1.4.0.0"),sQuery(id+"F0.wireOp",EDGE,"E1.4.0.1"),sQuery(id+"F0.wireOp",EDGE,"E1.4.0.2"),sQuery(id+"F0.wireOp",EDGE,"E1.4.0.3"),sQuery(id+"F0.wireOp",EDGE,"E2.0.5.0"),sQuery(id+"F0.wireOp",EDGE,"E2.3.5.0"),sQuery(id+"F0.wireOp",EDGE,"E2.6.5.0"),sQuery(id+"F0.wireOp",EDGE,"E2.9.5.0"),sQuery(id+"F0.wireOp",EDGE,"E3.bottom"),subQ0,sQuery(id+"F0.wireOp",EDGE,"E3.left"),sQuery(id+"F0.wireOp",EDGE,"E3.right")])],"isStart":false})],"blendedInto":[makeQuery(id+"F1.opExtrude","CAP_FACE",FACE,{"disambiguationData":[OSD([sQuery(id+"F0.wireOp",EDGE,"E0.bottom"),sQuery(id+"F0.wireOp",EDGE,"E0.top"),sQuery(id+"F0.wireOp",EDGE,"E0.left"),sQuery(id+"F0.wireOp",EDGE,"E0.right"),sQuery(id+"F0.wireOp",EDGE,"E1.1.0.0"),sQuery(id+"F0.wireOp",EDGE,"E1.1.0.1"),sQuery(id+"F0.wireOp",EDGE,"E1.1.0.2"),sQuery(id+"F0.wireOp",EDGE,"E1.1.0.3"),sQuery(id+"F0.wireOp",EDGE,"E1.2.0.0"),sQuery(id+"F0.wireOp",EDGE,"E1.2.0.1"),sQuery(id+"F0.wireOp",EDGE,"E1.2.0.2"),sQuery(id+"F0.wireOp",EDGE,"E1.2.0.3"),sQuery(id+"F0.wireOp",EDGE,"E1.3.0.0"),sQuery(id+"F0.wireOp",EDGE,"E1.3.0.1"),sQuery(id+"F0.wireOp",EDGE,"E1.3.0.2"),sQuery(id+"F0.wireOp",EDGE,"E1.3.0.3"),sQuery(id+"F0.wireOp",EDGE,"E1.4.0.0"),sQuery(id+"F0.wireOp",EDGE,"E1.4.0.1"),sQuery(id+"F0.wireOp",EDGE,"E1.4.0.2"),sQuery(id+"F0.wireOp",EDGE,"E1.4.0.3"),sQuery(id+"F0.wireOp",EDGE,"E2.0.5.0"),sQuery(id+"F0.wireOp",EDGE,"E2.3.5.0"),sQuery(id+"F0.wireOp",EDGE,"E2.6.5.0"),sQuery(id+"F0.wireOp",EDGE,"E2.9.5.0"),sQuery(id+"F0.wireOp",EDGE,"E3.bottom"),subQ0,sQuery(id+"F0.wireOp",EDGE,"E3.left"),sQuery(id+"F0.wireOp",EDGE,"E3.right")])],"isStart":false})]})],"fromTools":[makeQuery(id+"F18.opExtrude","CAP_EDGE",EDGE,{"disambiguationData":[OSD([sQuery(id+"F17.wireOp",EDGE,"E27.MirrorCS")])],"isStart":true})]});}
            var Q9;
            Q9=makeQuery(id+"F18.boolean.opBoolean","COPY",EDGE,{"derivedFrom":makeQuery(id+"F18.opExtrude","CAP_EDGE",EDGE,{"disambiguationData":[OSD([sQuery(id+"F17.wireOp",EDGE,"E26.MirrorCS")])],"isStart":true})});
            chamfer(context, id + "F19", {"entities" : qUnion([Q0, Q1, Q2, Q3, Q4, Q5, Q6, Q7, Q8, Q9]), "width" : 1.27 * mm, "tangentPropagation" : true});
        }
        {
            var Q0;
            Q0=makeQuery(id+"F4.boolean.opBoolean","MERGE",FACE,{"derivedFrom":[makeQuery(id+"F1.opExtrude","CAP_FACE",FACE,{"disambiguationData":[OSD([sQuery(id+"F0.wireOp",EDGE,"E0.bottom"),sQuery(id+"F0.wireOp",EDGE,"E0.top"),sQuery(id+"F0.wireOp",EDGE,"E0.left"),sQuery(id+"F0.wireOp",EDGE,"E0.right"),sQuery(id+"F0.wireOp",EDGE,"E1.1.0.0"),sQuery(id+"F0.wireOp",EDGE,"E1.1.0.1"),sQuery(id+"F0.wireOp",EDGE,"E1.1.0.2"),sQuery(id+"F0.wireOp",EDGE,"E1.1.0.3"),sQuery(id+"F0.wireOp",EDGE,"E1.2.0.0"),sQuery(id+"F0.wireOp",EDGE,"E1.2.0.1"),sQuery(id+"F0.wireOp",EDGE,"E1.2.0.2"),sQuery(id+"F0.wireOp",EDGE,"E1.2.0.3"),sQuery(id+"F0.wireOp",EDGE,"E1.3.0.0"),sQuery(id+"F0.wireOp",EDGE,"E1.3.0.1"),sQuery(id+"F0.wireOp",EDGE,"E1.3.0.2"),sQuery(id+"F0.wireOp",EDGE,"E1.3.0.3"),sQuery(id+"F0.wireOp",EDGE,"E1.4.0.0"),sQuery(id+"F0.wireOp",EDGE,"E1.4.0.1"),sQuery(id+"F0.wireOp",EDGE,"E1.4.0.2"),sQuery(id+"F0.wireOp",EDGE,"E1.4.0.3"),sQuery(id+"F0.wireOp",EDGE,"E2.0.5.0"),sQuery(id+"F0.wireOp",EDGE,"E2.3.5.0"),sQuery(id+"F0.wireOp",EDGE,"E2.6.5.0"),sQuery(id+"F0.wireOp",EDGE,"E2.9.5.0"),sQuery(id+"F0.wireOp",EDGE,"E3.bottom"),sQuery(id+"F0.wireOp",EDGE,"E3.top"),sQuery(id+"F0.wireOp",EDGE,"E3.left"),sQuery(id+"F0.wireOp",EDGE,"E3.right")])],"isStart":true}),makeQuery(id+"F4.opExtrude","CAP_FACE",FACE,{"disambiguationData":[OSD([sQuery(id+"F3.wireOp",EDGE,"E4.0"),sQuery(id+"F3.wireOp",EDGE,"E5.0"),sQuery(id+"F3.wireOp",EDGE,"E6.0"),sQuery(id+"F3.wireOp",EDGE,"E7.0")])],"isStart":true})]});
            var Q1;
            Q1=makeQuery(id+"F1.opExtrude","SWEPT_EDGE",EDGE,{"disambiguationData":[OSD([sQuery(id+"F0.wireOp",EDGE,"E3.bottom"),sQuery(id+"F0.wireOp",EDGE,"E3.left")])]});
            var Q2;
            Q2=makeQuery(id+"F1.opExtrude","SWEPT_EDGE",EDGE,{"disambiguationData":[OSD([sQuery(id+"F0.wireOp",EDGE,"E3.bottom"),sQuery(id+"F0.wireOp",EDGE,"E3.right")])]});
            chamfer(context, id + "F20", {"entities" : qUnion([Q0, Q1, Q2]), "width" : 3.17 * mm, "tangentPropagation" : true});
        }
        {
            var Q0;
            Q0=makeQuery(id+"F1.opExtrude","SWEPT_FACE",FACE,{"disambiguationData":[OSD([sQuery(id+"F0.wireOp",EDGE,"E3.top")])]});
            var sketch = newSketch(context, id + "F21", { "sketchPlane" : qUnion([Q0])});
            skLineSegment(sketch, "E31.bottom", {"start": v(-38.1, 60.33) * mm, "end": v(38.1, 60.33) * mm});
            skLineSegment(sketch, "E31.top", {"start": v(-38.1, 15.88) * mm, "end": v(38.1, 15.88) * mm});
            skLineSegment(sketch, "E31.left", {"start": v(-38.1, 60.33) * mm, "end": v(-38.1, 15.88) * mm});
            skLineSegment(sketch, "E31.right", {"start": v(38.1, 60.33) * mm, "end": v(38.1, 15.88) * mm});
            skSolve(sketch);
        }
        {
            var Q0;
            Q0=makeQuery(id+"F21.imprint","IMPRINT",FACE,{"disambiguationData":[TD([[makeQuery(id+"F21.imprint","IMPRINT",EDGE,{"derivedFrom":sQuery(id+"F21.wireOp",EDGE,"E31.bottom")}),-1.0]])]});
            extrude(context, id + "F22", {"entities" : qUnion([Q0]), "operationType" : NewBodyOperationType.REMOVE, "oppositeDirection" : true, "depth" : 12.7 * mm, "offsetDistance" : 25.4 * mm});
        }
        {
            var Q0;
            Q0=makeQuery(id+"F22.boolean.opBoolean","COPY",EDGE,{"derivedFrom":makeQuery(id+"F22.opExtrude","SWEPT_EDGE",EDGE,{"disambiguationData":[OSD([sQuery(id+"F21.wireOp",EDGE,"E31.bottom"),sQuery(id+"F21.wireOp",EDGE,"E31.right")])]})});
            var Q1;
            Q1=makeQuery(id+"F22.boolean.opBoolean","COPY",EDGE,{"derivedFrom":makeQuery(id+"F22.opExtrude","SWEPT_EDGE",EDGE,{"disambiguationData":[OSD([sQuery(id+"F21.wireOp",EDGE,"E31.bottom"),sQuery(id+"F21.wireOp",EDGE,"E31.left")])]})});
            chamfer(context, id + "F23", {"entities" : qUnion([Q0, Q1]), "width" : 25.4 * mm, "tangentPropagation" : true});
        }
        {
            var Q0;
            Q0=makeQuery(id+"F22.boolean.opBoolean","COPY",FACE,{"derivedFrom":makeQuery(id+"F22.opExtrude","CAP_FACE",FACE,{"disambiguationData":[OSD([sQuery(id+"F21.wireOp",EDGE,"E31.bottom"),sQuery(id+"F21.wireOp",EDGE,"E31.top"),sQuery(id+"F21.wireOp",EDGE,"E31.left"),sQuery(id+"F21.wireOp",EDGE,"E31.right")])],"isStart":false})});
            chamfer(context, id + "F24", {"entities" : qUnion([Q0]), "width" : 12.7 * mm, "tangentPropagation" : true});
        }
        {
            var Q0;
            Q0=makeQuery(id+"F2.opChamfer","BLEND_FACE",FACE,{"disambiguationData":[OSD([sQuery(id+"F0.wireOp",EDGE,"E3.bottom")])]});
            var sketch = newSketch(context, id + "F25", { "sketchPlane" : qUnion([Q0])});
            skLineSegment(sketch, "E32", {"start": v(-73.02, 62.2) * mm, "end": v(-57.15, 46.33) * mm});
            skLineSegment(sketch, "E33", {"start": v(-57.15, 46.33) * mm, "end": v(57.15, 46.33) * mm});
            skLineSegment(sketch, "E34", {"start": v(57.15, 46.33) * mm, "end": v(73.03, 62.2) * mm});
            skLineSegment(sketch, "E35", {"start": v(73.03, 62.2) * mm, "end": v(68.53, 62.2) * mm});
            skLineSegment(sketch, "E36", {"start": v(68.53, 62.2) * mm, "end": v(55.83, 49.5) * mm});
            skLineSegment(sketch, "E37", {"start": v(55.83, 49.5) * mm, "end": v(-55.83, 49.5) * mm});
            skLineSegment(sketch, "E38", {"start": v(-55.83, 49.5) * mm, "end": v(-68.53, 62.2) * mm});
            skLineSegment(sketch, "E39", {"start": v(-68.53, 62.2) * mm, "end": v(-73.02, 62.2) * mm});
            skLineSegment(sketch, "E40.0", {"start": v(85.73, 12.71) * mm, "end": v(85.73, 62.2) * mm, "construction": true});
            skLineSegment(sketch, "E41", {"start": v(85.73, 37.46) * mm, "end": v(78.34, 37.46) * mm, "construction": true});
            skLineSegment(sketch, "E42.MirrorCS", {"start": v(73.03, 12.71) * mm, "end": v(68.53, 12.71) * mm});
            skLineSegment(sketch, "E43.MirrorCS", {"start": v(-68.53, 12.71) * mm, "end": v(-73.02, 12.71) * mm});
            skLineSegment(sketch, "E44.MirrorCS", {"start": v(-73.02, 12.71) * mm, "end": v(-57.15, 28.59) * mm});
            skLineSegment(sketch, "E45.MirrorCS", {"start": v(-55.83, 25.41) * mm, "end": v(-68.53, 12.71) * mm});
            skLineSegment(sketch, "E46.MirrorCS", {"start": v(55.83, 25.41) * mm, "end": v(-55.83, 25.41) * mm});
            skLineSegment(sketch, "E47.MirrorCS", {"start": v(-57.15, 28.59) * mm, "end": v(57.15, 28.59) * mm});
            skLineSegment(sketch, "E48.MirrorCS", {"start": v(68.53, 12.71) * mm, "end": v(55.83, 25.41) * mm});
            skLineSegment(sketch, "E49.MirrorCS", {"start": v(57.15, 28.59) * mm, "end": v(73.03, 12.71) * mm});
            skSolve(sketch);
        }
        {
            var Q0;
            Q0 = qSketchRegion(id + "F25", true);
            extrude(context, id + "F26", {"entities" : qUnion([Q0]), "operationType" : NewBodyOperationType.REMOVE, "oppositeDirection" : true, "depth" : 1.27 * mm, "offsetDistance" : 25.4 * mm});
        }
        {
            var Q0;
            Q0=makeQuery(id+"F26.boolean.opBoolean","COPY",FACE,{"derivedFrom":makeQuery(id+"F26.opExtrude","CAP_FACE",FACE,{"disambiguationData":[OSD([sQuery(id+"F25.wireOp",EDGE,"E32"),sQuery(id+"F25.wireOp",EDGE,"E33"),sQuery(id+"F25.wireOp",EDGE,"E34"),sQuery(id+"F25.wireOp",EDGE,"E35"),sQuery(id+"F25.wireOp",EDGE,"E36"),sQuery(id+"F25.wireOp",EDGE,"E37"),sQuery(id+"F25.wireOp",EDGE,"E38"),sQuery(id+"F25.wireOp",EDGE,"E39")])],"isStart":false})});
            var Q1;
            Q1=makeQuery(id+"F26.boolean.opBoolean","COPY",FACE,{"derivedFrom":makeQuery(id+"F26.opExtrude","CAP_FACE",FACE,{"disambiguationData":[OSD([sQuery(id+"F25.wireOp",EDGE,"E42.MirrorCS"),sQuery(id+"F25.wireOp",EDGE,"E43.MirrorCS"),sQuery(id+"F25.wireOp",EDGE,"E44.MirrorCS"),sQuery(id+"F25.wireOp",EDGE,"E45.MirrorCS"),sQuery(id+"F25.wireOp",EDGE,"E46.MirrorCS"),sQuery(id+"F25.wireOp",EDGE,"E47.MirrorCS"),sQuery(id+"F25.wireOp",EDGE,"E48.MirrorCS"),sQuery(id+"F25.wireOp",EDGE,"E49.MirrorCS")])],"isStart":false})});
            fillet(context, id + "F27", {"entities" : qUnion([Q0, Q1]), "radius" : 1.27 * mm, "tangentPropagation" : true, "allowEdgeOverflow" : false});
        }
        {
            var Q0;
            Q0=makeQuery(id+"F4.boolean.opBoolean","MERGE",FACE,{"derivedFrom":[makeQuery(id+"F1.opExtrude","CAP_FACE",FACE,{"disambiguationData":[OSD([sQuery(id+"F0.wireOp",EDGE,"E0.bottom"),sQuery(id+"F0.wireOp",EDGE,"E0.top"),sQuery(id+"F0.wireOp",EDGE,"E0.left"),sQuery(id+"F0.wireOp",EDGE,"E0.right"),sQuery(id+"F0.wireOp",EDGE,"E1.1.0.0"),sQuery(id+"F0.wireOp",EDGE,"E1.1.0.1"),sQuery(id+"F0.wireOp",EDGE,"E1.1.0.2"),sQuery(id+"F0.wireOp",EDGE,"E1.1.0.3"),sQuery(id+"F0.wireOp",EDGE,"E1.2.0.0"),sQuery(id+"F0.wireOp",EDGE,"E1.2.0.1"),sQuery(id+"F0.wireOp",EDGE,"E1.2.0.2"),sQuery(id+"F0.wireOp",EDGE,"E1.2.0.3"),sQuery(id+"F0.wireOp",EDGE,"E1.3.0.0"),sQuery(id+"F0.wireOp",EDGE,"E1.3.0.1"),sQuery(id+"F0.wireOp",EDGE,"E1.3.0.2"),sQuery(id+"F0.wireOp",EDGE,"E1.3.0.3"),sQuery(id+"F0.wireOp",EDGE,"E1.4.0.0"),sQuery(id+"F0.wireOp",EDGE,"E1.4.0.1"),sQuery(id+"F0.wireOp",EDGE,"E1.4.0.2"),sQuery(id+"F0.wireOp",EDGE,"E1.4.0.3"),sQuery(id+"F0.wireOp",EDGE,"E2.0.5.0"),sQuery(id+"F0.wireOp",EDGE,"E2.3.5.0"),sQuery(id+"F0.wireOp",EDGE,"E2.6.5.0"),sQuery(id+"F0.wireOp",EDGE,"E2.9.5.0"),sQuery(id+"F0.wireOp",EDGE,"E3.bottom"),sQuery(id+"F0.wireOp",EDGE,"E3.top"),sQuery(id+"F0.wireOp",EDGE,"E3.left"),sQuery(id+"F0.wireOp",EDGE,"E3.right")])],"isStart":true}),makeQuery(id+"F4.opExtrude","CAP_FACE",FACE,{"disambiguationData":[OSD([sQuery(id+"F3.wireOp",EDGE,"E4.0"),sQuery(id+"F3.wireOp",EDGE,"E5.0"),sQuery(id+"F3.wireOp",EDGE,"E6.0"),sQuery(id+"F3.wireOp",EDGE,"E7.0")])],"isStart":true})]});
            cPlane(context, id + "F28", {"entities" : qUnion([Q0]), "cplaneType" : CPlaneType.OFFSET, "offset" : 25.4 * mm, "oppositeDirection" : true, "width" : 152.4 * mm, "height" : 152.4 * mm});
        }
        {
            var Q0;
            Q0=qCreatedBy(id+"F28.planeOp",FACE);
            var sketch = newSketch(context, id + "F29", { "sketchPlane" : qUnion([Q0])});
            skLineSegment(sketch, "E50.bottom", {"start": v(-86.36, 50.8) * mm, "end": v(86.36, 50.8) * mm});
            skLineSegment(sketch, "E50.top", {"start": v(-86.36, -50.8) * mm, "end": v(86.36, -50.8) * mm});
            skLineSegment(sketch, "E50.left", {"start": v(-88.9, 48.26) * mm, "end": v(-88.9, -48.26) * mm});
            skLineSegment(sketch, "E50.right", {"start": v(88.9, 48.26) * mm, "end": v(88.9, -48.26) * mm});
            skPoint(sketch, "E51.visualSharp", {"position": v(-88.9, 50.8) * mm});
            skArc(sketch, "E51.filletArc", {"start": v(-86.36, 50.8) * mm, "mid": v(-88.16, 50.06) * mm, "end": v(-88.9, 48.26) * mm});
            skPoint(sketch, "E52.visualSharp", {"position": v(-88.9, -50.8) * mm});
            skArc(sketch, "E52.filletArc", {"start": v(-88.9, -48.26) * mm, "mid": v(-88.16, -50.06) * mm, "end": v(-86.36, -50.8) * mm});
            skPoint(sketch, "E53.visualSharp", {"position": v(88.9, -50.8) * mm});
            skArc(sketch, "E53.filletArc", {"start": v(86.36, -50.8) * mm, "mid": v(88.16, -50.06) * mm, "end": v(88.9, -48.26) * mm});
            skPoint(sketch, "E54.visualSharp", {"position": v(88.9, 50.8) * mm});
            skArc(sketch, "E54.filletArc", {"start": v(88.9, 48.26) * mm, "mid": v(88.16, 50.06) * mm, "end": v(86.36, 50.8) * mm});
            skLineSegment(sketch, "E55.0", {"start": v(88.27, -46.35) * mm, "end": v(88.27, 46.35) * mm});
            skLineSegment(sketch, "E55.1", {"start": v(-84.46, -50.17) * mm, "end": v(84.45, -50.17) * mm});
            skLineSegment(sketch, "E55.2", {"start": v(-88.27, 46.36) * mm, "end": v(-88.27, -46.36) * mm});
            skLineSegment(sketch, "E55.3", {"start": v(84.45, 50.16) * mm, "end": v(-84.46, 50.17) * mm});
            skPoint(sketch, "E56.visualSharp", {"position": v(-88.27, -50.17) * mm});
            skArc(sketch, "E56.filletArc", {"start": v(-88.27, -46.36) * mm, "mid": v(-87.15, -49.05) * mm, "end": v(-84.46, -50.17) * mm});
            skPoint(sketch, "E57.visualSharp", {"position": v(88.27, -50.17) * mm});
            skArc(sketch, "E57.filletArc", {"start": v(84.45, -50.17) * mm, "mid": v(87.15, -49.05) * mm, "end": v(88.27, -46.36) * mm});
            skPoint(sketch, "E58.visualSharp", {"position": v(88.27, 50.16) * mm});
            skArc(sketch, "E58.filletArc", {"start": v(88.27, 46.35) * mm, "mid": v(87.15, 49.05) * mm, "end": v(84.45, 50.16) * mm});
            skPoint(sketch, "E59.visualSharp", {"position": v(-88.27, 50.17) * mm});
            skArc(sketch, "E59.filletArc", {"start": v(-84.46, 50.17) * mm, "mid": v(-87.15, 49.05) * mm, "end": v(-88.27, 46.36) * mm});
            skSolve(sketch);
        }
        {
            var Q0;
            Q0 = qSketchRegion(id + "F29", true);
            extrude(context, id + "F30", {"entities" : qUnion([Q0]), "operationType" : NewBodyOperationType.REMOVE, "depth" : 2.54 * mm, "offsetDistance" : 25.4 * mm});
        }
        {
            var Q0;
            Q0=makeQuery(id+"F9.boolean.opBoolean","COPY",FACE,{"derivedFrom":makeQuery(id+"F9.opExtrude","CAP_FACE",FACE,{"disambiguationData":[OSD([sQuery(id+"F8.wireOp",EDGE,"E12.0"),sQuery(id+"F8.wireOp",EDGE,"E12.1"),sQuery(id+"F8.wireOp",EDGE,"E12.2"),sQuery(id+"F8.wireOp",EDGE,"E12.3"),sQuery(id+"F8.wireOp",EDGE,"E12.4")])],"isStart":false})});
            var sketch = newSketch(context, id + "F31", { "sketchPlane" : qUnion([Q0])});
            skLineSegment(sketch, "E60.bottom", {"start": v(-25.08, 59.05) * mm, "end": v(25.08, 59.05) * mm});
            skLineSegment(sketch, "E60.top", {"start": v(-25.08, 38.1) * mm, "end": v(25.08, 38.1) * mm});
            skLineSegment(sketch, "E60.left", {"start": v(-25.08, 59.05) * mm, "end": v(-25.08, 38.1) * mm});
            skLineSegment(sketch, "E60.right", {"start": v(25.08, 59.05) * mm, "end": v(25.08, 38.1) * mm});
            skSolve(sketch);
        }
        {
            var Q0;
            Q0=makeQuery(id+"F31.imprint","IMPRINT",FACE,{"disambiguationData":[TD([[makeQuery(id+"F31.imprint","IMPRINT",EDGE,{"derivedFrom":sQuery(id+"F31.wireOp",EDGE,"E60.bottom")}),-1.0]])]});
            extrude(context, id + "F32", {"entities" : qUnion([Q0]), "operationType" : NewBodyOperationType.ADD, "depth" : 3.17 * mm, "offsetDistance" : 25.4 * mm});
        }
        {
            var Q0;
            Q0=makeQuery(id+"F32.opExtrude","CAP_FACE",FACE,{"disambiguationData":[OSD([sQuery(id+"F31.wireOp",EDGE,"E60.bottom"),sQuery(id+"F31.wireOp",EDGE,"E60.top"),sQuery(id+"F31.wireOp",EDGE,"E60.left"),sQuery(id+"F31.wireOp",EDGE,"E60.right")])],"isStart":false});
            var Q1;
            Q1=makeQuery(id+"F32.opExtrude","SWEPT_EDGE",EDGE,{"disambiguationData":[OSD([sQuery(id+"F31.wireOp",EDGE,"E60.bottom"),sQuery(id+"F31.wireOp",EDGE,"E60.left")])]});
            var Q2;
            Q2=makeQuery(id+"F32.opExtrude","SWEPT_EDGE",EDGE,{"disambiguationData":[OSD([sQuery(id+"F31.wireOp",EDGE,"E60.bottom"),sQuery(id+"F31.wireOp",EDGE,"E60.right")])]});
            var Q3;
            Q3=makeQuery(id+"F32.opExtrude","SWEPT_EDGE",EDGE,{"disambiguationData":[OSD([sQuery(id+"F31.wireOp",EDGE,"E60.top"),sQuery(id+"F31.wireOp",EDGE,"E60.right")])]});
            var Q4;
            Q4=makeQuery(id+"F32.opExtrude","SWEPT_EDGE",EDGE,{"disambiguationData":[OSD([sQuery(id+"F31.wireOp",EDGE,"E60.top"),sQuery(id+"F31.wireOp",EDGE,"E60.left")])]});
            chamfer(context, id + "F33", {"entities" : qUnion([Q0, Q1, Q2, Q3, Q4]), "width" : 3.17 * mm, "tangentPropagation" : true});
        }
        {
            var Q0;
            Q0=makeQuery(id+"F32.opExtrude","CAP_FACE",FACE,{"disambiguationData":[OSD([sQuery(id+"F31.wireOp",EDGE,"E60.bottom"),sQuery(id+"F31.wireOp",EDGE,"E60.top"),sQuery(id+"F31.wireOp",EDGE,"E60.left"),sQuery(id+"F31.wireOp",EDGE,"E60.right")])],"isStart":false});
            var sketch = newSketch(context, id + "F34", { "sketchPlane" : qUnion([Q0])});
            skLineSegment(sketch, "E61.bottom", {"start": v(-18.1, 54.6) * mm, "end": v(18.1, 54.6) * mm});
            skLineSegment(sketch, "E61.top", {"start": v(-18.1, 42.55) * mm, "end": v(18.1, 42.55) * mm});
            skLineSegment(sketch, "E61.left", {"start": v(-18.1, 54.6) * mm, "end": v(-18.1, 42.55) * mm});
            skLineSegment(sketch, "E61.right", {"start": v(18.1, 54.6) * mm, "end": v(18.1, 42.55) * mm});
            skSolve(sketch);
        }
        {
            var Q0;
            Q0=makeQuery(id+"F34.imprint","IMPRINT",FACE,{"disambiguationData":[TD([[makeQuery(id+"F34.imprint","IMPRINT",EDGE,{"derivedFrom":sQuery(id+"F34.wireOp",EDGE,"E61.bottom")}),-1.0]])]});
            extrude(context, id + "F35", {"entities" : qUnion([Q0]), "operationType" : NewBodyOperationType.REMOVE, "oppositeDirection" : true, "depth" : 6.35 * mm, "offsetDistance" : 25.4 * mm});
        }
        {
            var Q0;
            Q0=makeQuery(id+"F35.boolean.opBoolean","COPY",EDGE,{"derivedFrom":makeQuery(id+"F35.opExtrude","SWEPT_EDGE",EDGE,{"disambiguationData":[OSD([sQuery(id+"F34.wireOp",EDGE,"E61.bottom"),sQuery(id+"F34.wireOp",EDGE,"E61.right")])]})});
            var Q1;
            Q1=makeQuery(id+"F35.boolean.opBoolean","COPY",EDGE,{"derivedFrom":makeQuery(id+"F35.opExtrude","SWEPT_EDGE",EDGE,{"disambiguationData":[OSD([sQuery(id+"F34.wireOp",EDGE,"E61.bottom"),sQuery(id+"F34.wireOp",EDGE,"E61.left")])]})});
            chamfer(context, id + "F36", {"entities" : qUnion([Q0, Q1]), "width" : 5.08 * mm, "tangentPropagation" : true});
        }
        {
            var Q0;
            Q0=makeQuery(id+"F36.opChamfer","BLEND_EDGE",EDGE,{"blendedFrom":[makeQuery(id+"F35.boolean.opBoolean","COPY",EDGE,{"derivedFrom":makeQuery(id+"F35.opExtrude","SWEPT_EDGE",EDGE,{"disambiguationData":[OSD([sQuery(id+"F34.wireOp",EDGE,"E61.bottom"),sQuery(id+"F34.wireOp",EDGE,"E61.left")])]})}),makeQuery(id+"F32.opExtrude","CAP_FACE",FACE,{"disambiguationData":[OSD([sQuery(id+"F31.wireOp",EDGE,"E60.bottom"),sQuery(id+"F31.wireOp",EDGE,"E60.top"),sQuery(id+"F31.wireOp",EDGE,"E60.left"),sQuery(id+"F31.wireOp",EDGE,"E60.right")])],"isStart":false})],"blendedInto":[makeQuery(id+"F32.opExtrude","CAP_FACE",FACE,{"disambiguationData":[OSD([sQuery(id+"F31.wireOp",EDGE,"E60.bottom"),sQuery(id+"F31.wireOp",EDGE,"E60.top"),sQuery(id+"F31.wireOp",EDGE,"E60.left"),sQuery(id+"F31.wireOp",EDGE,"E60.right")])],"isStart":false})]});
            var Q1;
            Q1=makeQuery(id+"F36.opChamfer","BLEND_EDGE",EDGE,{"blendedFrom":[makeQuery(id+"F35.boolean.opBoolean","COPY",EDGE,{"derivedFrom":makeQuery(id+"F35.opExtrude","SWEPT_EDGE",EDGE,{"disambiguationData":[OSD([sQuery(id+"F34.wireOp",EDGE,"E61.bottom"),sQuery(id+"F34.wireOp",EDGE,"E61.right")])]})}),makeQuery(id+"F32.opExtrude","CAP_FACE",FACE,{"disambiguationData":[OSD([sQuery(id+"F31.wireOp",EDGE,"E60.bottom"),sQuery(id+"F31.wireOp",EDGE,"E60.top"),sQuery(id+"F31.wireOp",EDGE,"E60.left"),sQuery(id+"F31.wireOp",EDGE,"E60.right")])],"isStart":false})],"blendedInto":[makeQuery(id+"F32.opExtrude","CAP_FACE",FACE,{"disambiguationData":[OSD([sQuery(id+"F31.wireOp",EDGE,"E60.bottom"),sQuery(id+"F31.wireOp",EDGE,"E60.top"),sQuery(id+"F31.wireOp",EDGE,"E60.left"),sQuery(id+"F31.wireOp",EDGE,"E60.right")])],"isStart":false})]});
            var Q2;
            Q2=makeQuery(id+"F35.boolean.opBoolean","COPY",EDGE,{"derivedFrom":makeQuery(id+"F35.opExtrude","CAP_EDGE",EDGE,{"disambiguationData":[OSD([sQuery(id+"F34.wireOp",EDGE,"E61.top")])],"isStart":true})});
            var Q3;
            Q3=makeQuery(id+"F35.boolean.opBoolean","COPY",EDGE,{"derivedFrom":makeQuery(id+"F35.opExtrude","CAP_EDGE",EDGE,{"disambiguationData":[OSD([sQuery(id+"F34.wireOp",EDGE,"E61.right")])],"isStart":true})});
            var Q4;
            Q4=makeQuery(id+"F35.boolean.opBoolean","COPY",EDGE,{"derivedFrom":makeQuery(id+"F35.opExtrude","CAP_EDGE",EDGE,{"disambiguationData":[OSD([sQuery(id+"F34.wireOp",EDGE,"E61.left")])],"isStart":true})});
            var Q5;
            Q5=makeQuery(id+"F35.boolean.opBoolean","COPY",EDGE,{"derivedFrom":makeQuery(id+"F35.opExtrude","CAP_EDGE",EDGE,{"disambiguationData":[OSD([sQuery(id+"F34.wireOp",EDGE,"E61.bottom")])],"isStart":true})});
            var Q6;
            Q6=makeQuery(id+"F35.boolean.opBoolean","COPY",EDGE,{"derivedFrom":makeQuery(id+"F35.opExtrude","SWEPT_EDGE",EDGE,{"disambiguationData":[OSD([sQuery(id+"F34.wireOp",EDGE,"E61.top"),sQuery(id+"F34.wireOp",EDGE,"E61.left")])]})});
            var Q7;
            Q7=makeQuery(id+"F35.boolean.opBoolean","COPY",EDGE,{"derivedFrom":makeQuery(id+"F35.opExtrude","SWEPT_EDGE",EDGE,{"disambiguationData":[OSD([sQuery(id+"F34.wireOp",EDGE,"E61.top"),sQuery(id+"F34.wireOp",EDGE,"E61.right")])]})});
            fillet(context, id + "F37", {"entities" : qUnion([Q0, Q1, Q2, Q3, Q4, Q5, Q6, Q7]), "radius" : 1.27 * mm, "tangentPropagation" : true, "allowEdgeOverflow" : false});
        }
        {
            var Q0;
            Q0=makeQuery(id+"F30.boolean.opBoolean","COPY",EDGE,{"derivedFrom":makeQuery(id+"F30.opExtrude","CAP_EDGE",EDGE,{"disambiguationData":[OSD([sQuery(id+"F29.wireOp",EDGE,"E55.1")])],"isStart":true})});
            var Q1;
            {var subQ1=sQuery(id+"F29.wireOp",EDGE,"E55.0");Q1=makeQuery(id+"F30.boolean.opBoolean","COPY",EDGE,{"disambiguationData":[TD([makeQuery(id+"F13.opChamfer","BLEND_FACE",FACE,{"disambiguationData":[OSD([sQuery(id+"F11.wireOp",EDGE,"E13.3")])]})])],"derivedFrom":makeQuery(id+"F30.opExtrude","CAP_EDGE",EDGE,{"disambiguationData":[OSD([subQ1])],"isStart":true})});}
            var Q2;
            {var subQ1=sQuery(id+"F29.wireOp",EDGE,"E55.3");Q2=makeQuery(id+"F30.boolean.opBoolean","COPY",EDGE,{"disambiguationData":[TD([makeQuery(id+"F24.opChamfer","BLEND_FACE",FACE,{"disambiguationData":[OSD([sQuery(id+"F21.wireOp",EDGE,"E31.left")])]})])],"derivedFrom":makeQuery(id+"F30.opExtrude","CAP_EDGE",EDGE,{"disambiguationData":[OSD([subQ1])],"isStart":true})});}
            chamfer(context, id + "F38", {"entities" : qUnion([Q0, Q1, Q2]), "width" : 0.64 * mm, "tangentPropagation" : true});
        }
        {
            var Q0;
            Q0=makeQuery(id+"F12.boolean.opBoolean","COPY",FACE,{"derivedFrom":makeQuery(id+"F12.opExtrude","CAP_FACE",FACE,{"disambiguationData":[OSD([sQuery(id+"F11.wireOp",EDGE,"E13.0"),sQuery(id+"F11.wireOp",EDGE,"E13.1"),sQuery(id+"F11.wireOp",EDGE,"E13.2"),sQuery(id+"F11.wireOp",EDGE,"E13.3"),sQuery(id+"F11.wireOp",EDGE,"E13.4")])],"isStart":false})});
            var sketch = newSketch(context, id + "F39", { "sketchPlane" : qUnion([Q0])});
            skLineSegment(sketch, "E62.0", {"start": v(25.08, 59.05) * mm, "end": v(-25.08, 59.05) * mm});
            skLineSegment(sketch, "E63.0", {"start": v(25.08, 38.1) * mm, "end": v(-25.08, 38.1) * mm});
            skLineSegment(sketch, "E64.0", {"start": v(25.08, 59.05) * mm, "end": v(25.08, 38.1) * mm});
            skLineSegment(sketch, "E65.0", {"start": v(-25.08, 59.05) * mm, "end": v(-25.08, 38.1) * mm});
            skPoint(sketch, "E66.orphan", {"position": v(25.08, 55.88) * mm});
            skPoint(sketch, "E67.orphan", {"position": v(25.08, 41.27) * mm});
            skPoint(sketch, "E68.orphan", {"position": v(-21.9, 59.05) * mm});
            skPoint(sketch, "E69.orphan", {"position": v(-25.08, 41.28) * mm});
            skPoint(sketch, "E70.orphan", {"position": v(21.9, 38.1) * mm});
            skPoint(sketch, "E71.orphan", {"position": v(21.9, 59.05) * mm});
            skPoint(sketch, "E72.orphan", {"position": v(-25.08, 55.88) * mm});
            skPoint(sketch, "E73.orphan", {"position": v(-21.9, 38.1) * mm});
            skSolve(sketch);
        }
        {
            var Q0;
            Q0=makeQuery(id+"F39.imprint","IMPRINT",FACE,{"disambiguationData":[TD([[makeQuery(id+"F39.imprint","IMPRINT",EDGE,{"derivedFrom":sQuery(id+"F39.wireOp",EDGE,"E62.0")}),1.0]])]});
            extrude(context, id + "F40", {"entities" : qUnion([Q0]), "operationType" : NewBodyOperationType.ADD, "depth" : 3.17 * mm, "offsetDistance" : 25.4 * mm});
        }
        {
            var Q0;
            Q0=makeQuery(id+"F40.opExtrude","CAP_FACE",FACE,{"disambiguationData":[OSD([sQuery(id+"F39.wireOp",EDGE,"E62.0"),sQuery(id+"F39.wireOp",EDGE,"E63.0"),sQuery(id+"F39.wireOp",EDGE,"E64.0"),sQuery(id+"F39.wireOp",EDGE,"E65.0")])],"isStart":false});
            var Q1;
            Q1=makeQuery(id+"F40.opExtrude","SWEPT_EDGE",EDGE,{"disambiguationData":[OSD([sQuery(id+"F39.wireOp",EDGE,"E62.0"),sQuery(id+"F39.wireOp",EDGE,"E64.0")])]});
            var Q2;
            Q2=makeQuery(id+"F40.opExtrude","SWEPT_EDGE",EDGE,{"disambiguationData":[OSD([sQuery(id+"F39.wireOp",EDGE,"E62.0"),sQuery(id+"F39.wireOp",EDGE,"E65.0")])]});
            var Q3;
            Q3=makeQuery(id+"F40.opExtrude","SWEPT_EDGE",EDGE,{"disambiguationData":[OSD([sQuery(id+"F39.wireOp",EDGE,"E63.0"),sQuery(id+"F39.wireOp",EDGE,"E65.0")])]});
            var Q4;
            Q4=makeQuery(id+"F40.opExtrude","SWEPT_EDGE",EDGE,{"disambiguationData":[OSD([sQuery(id+"F39.wireOp",EDGE,"E63.0"),sQuery(id+"F39.wireOp",EDGE,"E64.0")])]});
            chamfer(context, id + "F41", {"entities" : qUnion([Q0, Q1, Q2, Q3, Q4]), "width" : 3.17 * mm, "tangentPropagation" : true});
        }
        {
            var Q0;
            Q0=makeQuery(id+"F40.opExtrude","CAP_FACE",FACE,{"disambiguationData":[OSD([sQuery(id+"F39.wireOp",EDGE,"E62.0"),sQuery(id+"F39.wireOp",EDGE,"E63.0"),sQuery(id+"F39.wireOp",EDGE,"E64.0"),sQuery(id+"F39.wireOp",EDGE,"E65.0")])],"isStart":false});
            var sketch = newSketch(context, id + "F42", { "sketchPlane" : qUnion([Q0])});
            skLineSegment(sketch, "E74.0", {"start": v(-18.1, 42.55) * mm, "end": v(-18.1, 54.6) * mm});
            skLineSegment(sketch, "E75.0", {"start": v(18.1, 42.55) * mm, "end": v(-18.1, 42.55) * mm});
            skLineSegment(sketch, "E76.0", {"start": v(-18.1, 54.6) * mm, "end": v(18.1, 54.6) * mm});
            skPoint(sketch, "E77.0", {"position": v(18.1, 46.67) * mm});
            skPoint(sketch, "E78.0", {"position": v(18.1, 43.81) * mm});
            skLineSegment(sketch, "E79.0", {"start": v(18.1, 54.6) * mm, "end": v(18.1, 42.54) * mm});
            skPoint(sketch, "E80.orphan", {"position": v(-18.1, 49.53) * mm});
            skPoint(sketch, "E81.orphan", {"position": v(18.1, 49.53) * mm});
            skPoint(sketch, "E82.orphan", {"position": v(16.83, 42.54) * mm});
            skPoint(sketch, "E83.orphan", {"position": v(-16.83, 42.55) * mm});
            skPoint(sketch, "E84.orphan", {"position": v(-18.1, 43.81) * mm});
            skPoint(sketch, "E85.orphan", {"position": v(13.02, 54.6) * mm});
            skPoint(sketch, "E86.orphan", {"position": v(-13.02, 54.6) * mm});
            skSolve(sketch);
        }
        {
            var Q0;
            Q0=makeQuery(id+"F42.imprint","IMPRINT",FACE,{"disambiguationData":[TD([[makeQuery(id+"F42.imprint","IMPRINT",EDGE,{"derivedFrom":sQuery(id+"F42.wireOp",EDGE,"E74.0")}),-1.0]])]});
            extrude(context, id + "F43", {"entities" : qUnion([Q0]), "operationType" : NewBodyOperationType.REMOVE, "oppositeDirection" : true, "depth" : 6.35 * mm, "offsetDistance" : 25.4 * mm});
        }
        {
            var Q0;
            Q0=makeQuery(id+"F43.boolean.opBoolean","COPY",EDGE,{"derivedFrom":makeQuery(id+"F43.opExtrude","SWEPT_EDGE",EDGE,{"disambiguationData":[OSD([sQuery(id+"F42.wireOp",EDGE,"E74.0"),sQuery(id+"F42.wireOp",EDGE,"E76.0")])]})});
            var Q1;
            Q1=makeQuery(id+"F43.boolean.opBoolean","COPY",EDGE,{"derivedFrom":makeQuery(id+"F43.opExtrude","SWEPT_EDGE",EDGE,{"disambiguationData":[OSD([sQuery(id+"F42.wireOp",EDGE,"E76.0"),sQuery(id+"F42.wireOp",EDGE,"E79.0")])]})});
            chamfer(context, id + "F44", {"entities" : qUnion([Q0, Q1]), "width" : 5.08 * mm, "tangentPropagation" : true});
        }
        {
            var Q0;
            Q0=makeQuery(id+"F43.boolean.opBoolean","COPY",EDGE,{"derivedFrom":makeQuery(id+"F43.opExtrude","CAP_EDGE",EDGE,{"disambiguationData":[OSD([sQuery(id+"F42.wireOp",EDGE,"E76.0")])],"isStart":true})});
            var Q1;
            Q1=makeQuery(id+"F44.opChamfer","BLEND_EDGE",EDGE,{"blendedFrom":[makeQuery(id+"F43.boolean.opBoolean","COPY",EDGE,{"derivedFrom":makeQuery(id+"F43.opExtrude","SWEPT_EDGE",EDGE,{"disambiguationData":[OSD([sQuery(id+"F42.wireOp",EDGE,"E76.0"),sQuery(id+"F42.wireOp",EDGE,"E79.0")])]})}),makeQuery(id+"F40.opExtrude","CAP_FACE",FACE,{"disambiguationData":[OSD([sQuery(id+"F39.wireOp",EDGE,"E62.0"),sQuery(id+"F39.wireOp",EDGE,"E63.0"),sQuery(id+"F39.wireOp",EDGE,"E64.0"),sQuery(id+"F39.wireOp",EDGE,"E65.0")])],"isStart":false})],"blendedInto":[makeQuery(id+"F40.opExtrude","CAP_FACE",FACE,{"disambiguationData":[OSD([sQuery(id+"F39.wireOp",EDGE,"E62.0"),sQuery(id+"F39.wireOp",EDGE,"E63.0"),sQuery(id+"F39.wireOp",EDGE,"E64.0"),sQuery(id+"F39.wireOp",EDGE,"E65.0")])],"isStart":false})]});
            var Q2;
            Q2=makeQuery(id+"F43.boolean.opBoolean","COPY",EDGE,{"derivedFrom":makeQuery(id+"F43.opExtrude","CAP_EDGE",EDGE,{"disambiguationData":[OSD([sQuery(id+"F42.wireOp",EDGE,"E79.0")])],"isStart":true})});
            var Q3;
            Q3=makeQuery(id+"F43.boolean.opBoolean","COPY",EDGE,{"derivedFrom":makeQuery(id+"F43.opExtrude","CAP_EDGE",EDGE,{"disambiguationData":[OSD([sQuery(id+"F42.wireOp",EDGE,"E75.0")])],"isStart":true})});
            var Q4;
            Q4=makeQuery(id+"F43.boolean.opBoolean","COPY",EDGE,{"derivedFrom":makeQuery(id+"F43.opExtrude","CAP_EDGE",EDGE,{"disambiguationData":[OSD([sQuery(id+"F42.wireOp",EDGE,"E74.0")])],"isStart":true})});
            var Q5;
            Q5=makeQuery(id+"F44.opChamfer","BLEND_EDGE",EDGE,{"blendedFrom":[makeQuery(id+"F43.boolean.opBoolean","COPY",EDGE,{"derivedFrom":makeQuery(id+"F43.opExtrude","SWEPT_EDGE",EDGE,{"disambiguationData":[OSD([sQuery(id+"F42.wireOp",EDGE,"E74.0"),sQuery(id+"F42.wireOp",EDGE,"E76.0")])]})}),makeQuery(id+"F40.opExtrude","CAP_FACE",FACE,{"disambiguationData":[OSD([sQuery(id+"F39.wireOp",EDGE,"E62.0"),sQuery(id+"F39.wireOp",EDGE,"E63.0"),sQuery(id+"F39.wireOp",EDGE,"E64.0"),sQuery(id+"F39.wireOp",EDGE,"E65.0")])],"isStart":false})],"blendedInto":[makeQuery(id+"F40.opExtrude","CAP_FACE",FACE,{"disambiguationData":[OSD([sQuery(id+"F39.wireOp",EDGE,"E62.0"),sQuery(id+"F39.wireOp",EDGE,"E63.0"),sQuery(id+"F39.wireOp",EDGE,"E64.0"),sQuery(id+"F39.wireOp",EDGE,"E65.0")])],"isStart":false})]});
            fillet(context, id + "F45", {"entities" : qUnion([Q0, Q1, Q2, Q3, Q4, Q5]), "radius" : 1.27 * mm, "tangentPropagation" : true, "allowEdgeOverflow" : false});
        }
        {
            var Q0;
            Q0=makeQuery(id+"F43.boolean.opBoolean","COPY",FACE,{"derivedFrom":makeQuery(id+"F43.opExtrude","CAP_FACE",FACE,{"disambiguationData":[OSD([sQuery(id+"F42.wireOp",EDGE,"E74.0"),sQuery(id+"F42.wireOp",EDGE,"E75.0"),sQuery(id+"F42.wireOp",EDGE,"E76.0"),sQuery(id+"F42.wireOp",EDGE,"E79.0")])],"isStart":false})});
            var Q1;
            Q1=makeQuery(id+"F35.boolean.opBoolean","COPY",FACE,{"derivedFrom":makeQuery(id+"F35.opExtrude","CAP_FACE",FACE,{"disambiguationData":[OSD([sQuery(id+"F34.wireOp",EDGE,"E61.bottom"),sQuery(id+"F34.wireOp",EDGE,"E61.top"),sQuery(id+"F34.wireOp",EDGE,"E61.left"),sQuery(id+"F34.wireOp",EDGE,"E61.right")])],"isStart":false})});
            chamfer(context, id + "F46", {"entities" : qUnion([Q0, Q1]), "width" : 1.27 * mm, "tangentPropagation" : true});
        }
        {
            var Q0;
            Q0=qCreatedBy(makeId("Front.planeOp"),FACE);
            var sketch = newSketch(context, id + "F47", { "sketchPlane" : qUnion([Q0])});
            skLineSegment(sketch, "E87", {"start": v(0, 0) * mm, "end": v(0, 112.8) * mm, "construction": true});
            skSolve(sketch);
        }
        {
            var Q0;
            Q0=makeQuery(id+"F1.opExtrude","SWEPT_BODY",BODY,{"disambiguationData":[OSD([sQuery(id+"F0.wireOp",EDGE,"E0.bottom"),sQuery(id+"F0.wireOp",EDGE,"E0.top"),sQuery(id+"F0.wireOp",EDGE,"E0.left"),sQuery(id+"F0.wireOp",EDGE,"E0.right"),sQuery(id+"F0.wireOp",EDGE,"E1.1.0.0"),sQuery(id+"F0.wireOp",EDGE,"E1.1.0.1"),sQuery(id+"F0.wireOp",EDGE,"E1.1.0.2"),sQuery(id+"F0.wireOp",EDGE,"E1.1.0.3"),sQuery(id+"F0.wireOp",EDGE,"E1.2.0.0"),sQuery(id+"F0.wireOp",EDGE,"E1.2.0.1"),sQuery(id+"F0.wireOp",EDGE,"E1.2.0.2"),sQuery(id+"F0.wireOp",EDGE,"E1.2.0.3"),sQuery(id+"F0.wireOp",EDGE,"E1.3.0.0"),sQuery(id+"F0.wireOp",EDGE,"E1.3.0.1"),sQuery(id+"F0.wireOp",EDGE,"E1.3.0.2"),sQuery(id+"F0.wireOp",EDGE,"E1.3.0.3"),sQuery(id+"F0.wireOp",EDGE,"E1.4.0.0"),sQuery(id+"F0.wireOp",EDGE,"E1.4.0.1"),sQuery(id+"F0.wireOp",EDGE,"E1.4.0.2"),sQuery(id+"F0.wireOp",EDGE,"E1.4.0.3"),sQuery(id+"F0.wireOp",EDGE,"E2.0.5.0"),sQuery(id+"F0.wireOp",EDGE,"E2.3.5.0"),sQuery(id+"F0.wireOp",EDGE,"E2.6.5.0"),sQuery(id+"F0.wireOp",EDGE,"E2.9.5.0"),sQuery(id+"F0.wireOp",EDGE,"E3.bottom"),sQuery(id+"F0.wireOp",EDGE,"E3.top"),sQuery(id+"F0.wireOp",EDGE,"E3.left"),sQuery(id+"F0.wireOp",EDGE,"E3.right")])]});
            var Q1;
            Q1=sQuery(id+"F47.wireOp",EDGE,"E87");
            transform(context, id + "F48", {"entities" : qUnion([Q0]), "transformType" : TransformType.ROTATION, "transformAxis" : qUnion([Q1]), "angle" : 180 * degree, "makeCopy" : false});
        }
        {
            var Q0;
            Q0=makeQuery(id+"F1.opExtrude","CAP_FACE",FACE,{"disambiguationData":[OSD([sQuery(id+"F0.wireOp",EDGE,"E0.bottom"),sQuery(id+"F0.wireOp",EDGE,"E0.top"),sQuery(id+"F0.wireOp",EDGE,"E0.left"),sQuery(id+"F0.wireOp",EDGE,"E0.right"),sQuery(id+"F0.wireOp",EDGE,"E1.1.0.0"),sQuery(id+"F0.wireOp",EDGE,"E1.1.0.1"),sQuery(id+"F0.wireOp",EDGE,"E1.1.0.2"),sQuery(id+"F0.wireOp",EDGE,"E1.1.0.3"),sQuery(id+"F0.wireOp",EDGE,"E1.2.0.0"),sQuery(id+"F0.wireOp",EDGE,"E1.2.0.1"),sQuery(id+"F0.wireOp",EDGE,"E1.2.0.2"),sQuery(id+"F0.wireOp",EDGE,"E1.2.0.3"),sQuery(id+"F0.wireOp",EDGE,"E1.3.0.0"),sQuery(id+"F0.wireOp",EDGE,"E1.3.0.1"),sQuery(id+"F0.wireOp",EDGE,"E1.3.0.2"),sQuery(id+"F0.wireOp",EDGE,"E1.3.0.3"),sQuery(id+"F0.wireOp",EDGE,"E1.4.0.0"),sQuery(id+"F0.wireOp",EDGE,"E1.4.0.1"),sQuery(id+"F0.wireOp",EDGE,"E1.4.0.2"),sQuery(id+"F0.wireOp",EDGE,"E1.4.0.3"),sQuery(id+"F0.wireOp",EDGE,"E2.0.5.0"),sQuery(id+"F0.wireOp",EDGE,"E2.3.5.0"),sQuery(id+"F0.wireOp",EDGE,"E2.6.5.0"),sQuery(id+"F0.wireOp",EDGE,"E2.9.5.0"),sQuery(id+"F0.wireOp",EDGE,"E3.bottom"),sQuery(id+"F0.wireOp",EDGE,"E3.top"),sQuery(id+"F0.wireOp",EDGE,"E3.left"),sQuery(id+"F0.wireOp",EDGE,"E3.right")])],"isStart":false});
            var sketch = newSketch(context, id + "F49", { "sketchPlane" : qUnion([Q0])});
            skLineSegment(sketch, "E88.0.0", {"start": v(-63.5, 50.8) * mm, "end": v(-63.5, 47.62) * mm, "construction": true});
            skLineSegment(sketch, "E88.0.1", {"start": v(-63.5, 47.62) * mm, "end": v(-69.85, 47.62) * mm, "construction": true});
            skLineSegment(sketch, "E88.0.2", {"start": v(-69.85, 47.62) * mm, "end": v(-69.85, 41.28) * mm, "construction": true});
            skLineSegment(sketch, "E88.0.3", {"start": v(-69.85, 41.28) * mm, "end": v(-50.8, 41.28) * mm, "construction": true});
            skLineSegment(sketch, "E88.0.4", {"start": v(-50.8, 41.28) * mm, "end": v(-50.8, 47.62) * mm, "construction": true});
            skLineSegment(sketch, "E88.0.5", {"start": v(-50.8, 47.62) * mm, "end": v(-57.15, 47.62) * mm, "construction": true});
            skLineSegment(sketch, "E88.0.6", {"start": v(-57.15, 47.62) * mm, "end": v(-57.15, 50.8) * mm, "construction": true});
            skLineSegment(sketch, "E88.0.7", {"start": v(-57.15, 50.8) * mm, "end": v(-63.5, 50.8) * mm, "construction": true});
            skLineSegment(sketch, "E89.0.0", {"start": v(50.8, 47.63) * mm, "end": v(50.8, 41.28) * mm, "construction": true});
            skLineSegment(sketch, "E89.0.1", {"start": v(50.8, 41.28) * mm, "end": v(69.85, 41.28) * mm, "construction": true});
            skLineSegment(sketch, "E89.0.2", {"start": v(69.85, 41.28) * mm, "end": v(69.85, 47.63) * mm, "construction": true});
            skLineSegment(sketch, "E89.0.3", {"start": v(69.85, 47.63) * mm, "end": v(63.5, 47.63) * mm, "construction": true});
            skLineSegment(sketch, "E89.0.4", {"start": v(63.5, 47.63) * mm, "end": v(63.5, 50.8) * mm, "construction": true});
            skLineSegment(sketch, "E89.0.5", {"start": v(63.5, 50.8) * mm, "end": v(57.15, 50.8) * mm, "construction": true});
            skLineSegment(sketch, "E89.0.6", {"start": v(57.15, 50.8) * mm, "end": v(57.15, 47.63) * mm, "construction": true});
            skLineSegment(sketch, "E89.0.7", {"start": v(57.15, 47.63) * mm, "end": v(50.8, 47.63) * mm, "construction": true});
            skLineSegment(sketch, "E90.0", {"start": v(-57.4, 50.55) * mm, "end": v(-63.25, 50.55) * mm});
            skLineSegment(sketch, "E90.1", {"start": v(-57.4, 47.37) * mm, "end": v(-57.4, 50.55) * mm});
            skLineSegment(sketch, "E90.2", {"start": v(-63.25, 50.55) * mm, "end": v(-63.25, 47.37) * mm});
            skLineSegment(sketch, "E90.3", {"start": v(-51.05, 47.37) * mm, "end": v(-57.4, 47.37) * mm});
            skLineSegment(sketch, "E90.4", {"start": v(-63.25, 47.37) * mm, "end": v(-69.6, 47.37) * mm});
            skLineSegment(sketch, "E90.5", {"start": v(-69.6, 47.37) * mm, "end": v(-69.6, 41.53) * mm});
            skLineSegment(sketch, "E90.6", {"start": v(-69.6, 41.53) * mm, "end": v(-51.05, 41.53) * mm});
            skLineSegment(sketch, "E90.7", {"start": v(-51.05, 41.53) * mm, "end": v(-51.05, 47.37) * mm});
            skLineSegment(sketch, "E91.MirrorCS", {"start": v(63.25, 47.37) * mm, "end": v(69.6, 47.37) * mm});
            skLineSegment(sketch, "E92.MirrorCS", {"start": v(69.6, 47.37) * mm, "end": v(69.6, 41.53) * mm});
            skLineSegment(sketch, "E93.MirrorCS", {"start": v(69.6, 41.53) * mm, "end": v(51.05, 41.53) * mm});
            skLineSegment(sketch, "E94.MirrorCS", {"start": v(51.05, 41.53) * mm, "end": v(51.05, 47.37) * mm});
            skLineSegment(sketch, "E95.MirrorCS", {"start": v(51.05, 47.37) * mm, "end": v(57.4, 47.37) * mm});
            skLineSegment(sketch, "E96.MirrorCS", {"start": v(57.4, 47.37) * mm, "end": v(57.4, 50.55) * mm});
            skLineSegment(sketch, "E97.MirrorCS", {"start": v(63.25, 50.55) * mm, "end": v(63.25, 47.37) * mm});
            skLineSegment(sketch, "E98.MirrorCS", {"start": v(57.4, 50.55) * mm, "end": v(63.25, 50.55) * mm});
            skSolve(sketch);
        }
        {
            var Q0;
            Q0=makeQuery(id+"F49.imprint","IMPRINT",FACE,{"disambiguationData":[TD([[makeQuery(id+"F49.imprint","IMPRINT",EDGE,{"derivedFrom":sQuery(id+"F49.wireOp",EDGE,"E90.0")}),1.0]])]});
            var Q1;
            Q1=makeQuery(id+"F49.imprint","IMPRINT",FACE,{"disambiguationData":[TD([[makeQuery(id+"F49.imprint","IMPRINT",EDGE,{"derivedFrom":sQuery(id+"F49.wireOp",EDGE,"E91.MirrorCS")}),-1.0]])]});
            extrude(context, id + "F50", {"entities" : qUnion([Q0, Q1]), "oppositeDirection" : true, "depth" : 36.83 * mm, "offsetDistance" : 25.4 * mm});
        }
        {
            var Q0;
            Q0=makeQuery(id+"F4.boolean.opBoolean","MERGE",FACE,{"derivedFrom":[makeQuery(id+"F1.opExtrude","CAP_FACE",FACE,{"disambiguationData":[OSD([sQuery(id+"F0.wireOp",EDGE,"E0.bottom"),sQuery(id+"F0.wireOp",EDGE,"E0.top"),sQuery(id+"F0.wireOp",EDGE,"E0.left"),sQuery(id+"F0.wireOp",EDGE,"E0.right"),sQuery(id+"F0.wireOp",EDGE,"E1.1.0.0"),sQuery(id+"F0.wireOp",EDGE,"E1.1.0.1"),sQuery(id+"F0.wireOp",EDGE,"E1.1.0.2"),sQuery(id+"F0.wireOp",EDGE,"E1.1.0.3"),sQuery(id+"F0.wireOp",EDGE,"E1.2.0.0"),sQuery(id+"F0.wireOp",EDGE,"E1.2.0.1"),sQuery(id+"F0.wireOp",EDGE,"E1.2.0.2"),sQuery(id+"F0.wireOp",EDGE,"E1.2.0.3"),sQuery(id+"F0.wireOp",EDGE,"E1.3.0.0"),sQuery(id+"F0.wireOp",EDGE,"E1.3.0.1"),sQuery(id+"F0.wireOp",EDGE,"E1.3.0.2"),sQuery(id+"F0.wireOp",EDGE,"E1.3.0.3"),sQuery(id+"F0.wireOp",EDGE,"E1.4.0.0"),sQuery(id+"F0.wireOp",EDGE,"E1.4.0.1"),sQuery(id+"F0.wireOp",EDGE,"E1.4.0.2"),sQuery(id+"F0.wireOp",EDGE,"E1.4.0.3"),sQuery(id+"F0.wireOp",EDGE,"E2.0.5.0"),sQuery(id+"F0.wireOp",EDGE,"E2.3.5.0"),sQuery(id+"F0.wireOp",EDGE,"E2.6.5.0"),sQuery(id+"F0.wireOp",EDGE,"E2.9.5.0"),sQuery(id+"F0.wireOp",EDGE,"E3.bottom"),sQuery(id+"F0.wireOp",EDGE,"E3.top"),sQuery(id+"F0.wireOp",EDGE,"E3.left"),sQuery(id+"F0.wireOp",EDGE,"E3.right")])],"isStart":true}),makeQuery(id+"F4.opExtrude","CAP_FACE",FACE,{"disambiguationData":[OSD([sQuery(id+"F3.wireOp",EDGE,"E4.0"),sQuery(id+"F3.wireOp",EDGE,"E5.0"),sQuery(id+"F3.wireOp",EDGE,"E6.0"),sQuery(id+"F3.wireOp",EDGE,"E7.0")])],"isStart":true})]});
            var sketch = newSketch(context, id + "F51", { "sketchPlane" : qUnion([Q0])});
            skText(sketch, "E99", { "text": "COMMISSIONED BY: \nWES DELEO\n\nTSI, 2017", "fontName": "AllertaStencil-Regular.ttf"});
            const initialGuessF51  = {"E99": [-0.0844, 0.02579, 1, 0, 0.01301]};
            skSetInitialGuess(sketch, initialGuessF51);
            skSolve(sketch);
        }
        {
            var Q0;
            Q0 = qSketchRegion(id + "F51", true);
            extrude(context, id + "F52", {"entities" : qUnion([Q0]), "operationType" : NewBodyOperationType.REMOVE, "oppositeDirection" : true, "depth" : 1.27 * mm, "offsetDistance" : 25.4 * mm});
        }
    });
